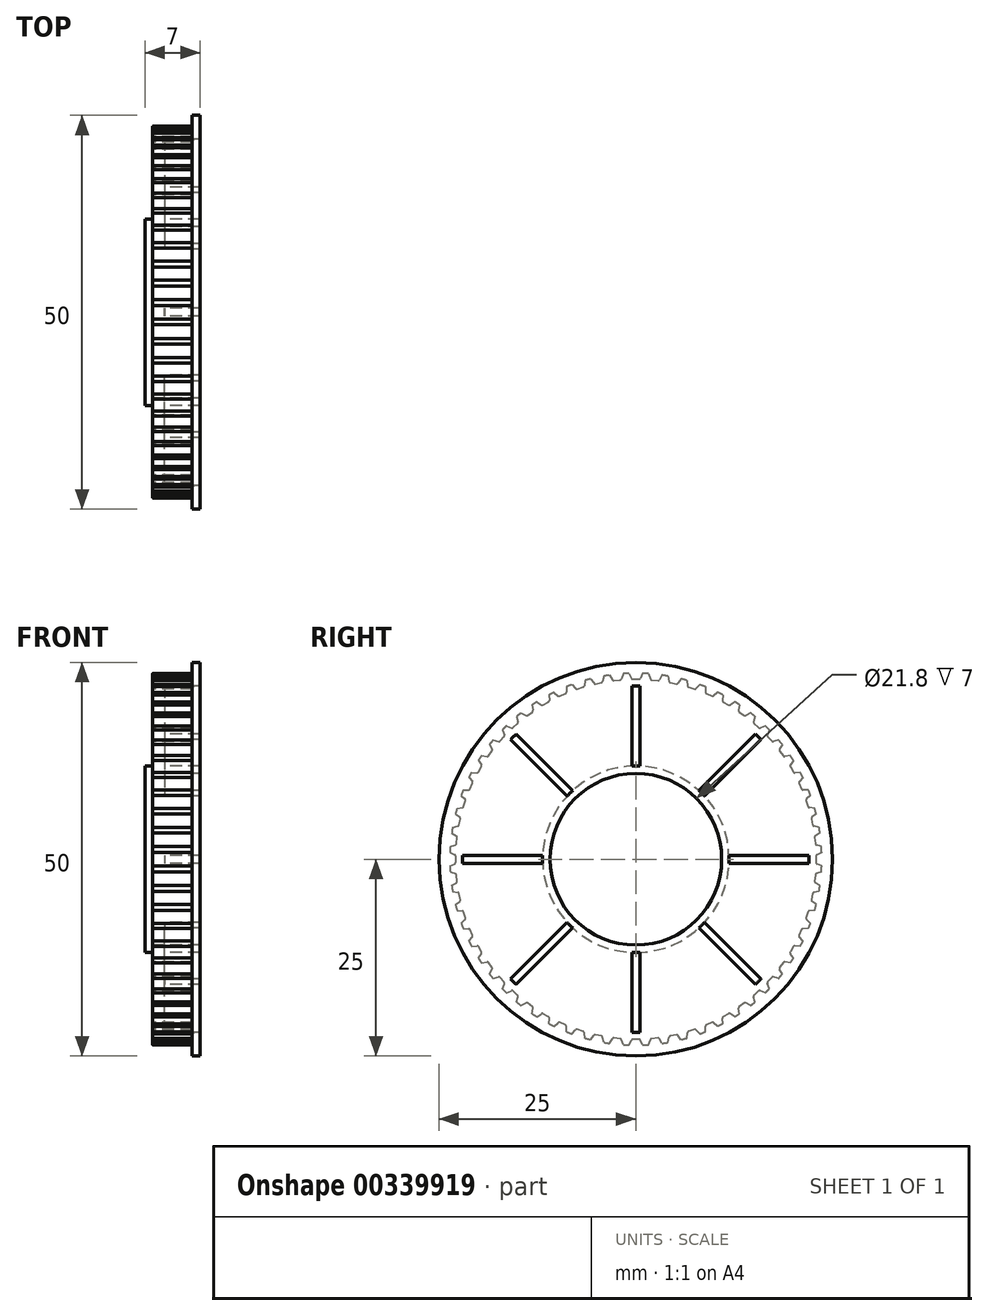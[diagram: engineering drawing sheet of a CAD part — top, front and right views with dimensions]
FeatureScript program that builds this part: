
annotation { "Feature Type Name" : "Feature", "Feature Type Description" : "" }
export const myFeature = defineFeature(function(context is Context, id is Id, definition is map)
    precondition{}
    {
        {
            var Q0;
            Q0=qCreatedBy(makeId("Right.planeOp"),FACE);
            var sketch = newSketch(context, id + "F0", { "sketchPlane" : qUnion([Q0])});
            skCircle(sketch, "E0.0", {"center": v(0, 0) * mm, "radius": 17.8 * mm});
            skCircle(sketch, "E1", {"center": v(0, 0) * mm, "radius": 25 * mm});
            skCircle(sketch, "E2", {"center": v(0, 0) * mm, "radius": 23.86 * mm});
            skCircle(sketch, "E3", {"center": v(0, 0) * mm, "radius": 23.62 * mm});
            skLineSegment(sketch, "E4", {"start": v(-0.88, 23.62) * mm, "end": v(0.87, 23.62) * mm});
            skLineSegment(sketch, "E5", {"start": v(0, 18.78) * mm, "end": v(0, 27.09) * mm, "construction": true});
            skLineSegment(sketch, "E6", {"start": v(-0.4, 22.88) * mm, "end": v(0.4, 22.88) * mm});
            skLineSegment(sketch, "E7", {"start": v(-0.87, 23.62) * mm, "end": v(-0.58, 23) * mm});
            skLineSegment(sketch, "E8", {"start": v(0.87, 23.62) * mm, "end": v(0.58, 23) * mm});
            skArc(sketch, "E9.filletArc", {"start": v(0.4, 22.88) * mm, "mid": v(0.5, 22.9) * mm, "end": v(0.58, 23) * mm});
            skArc(sketch, "E10.filletArc", {"start": v(-0.58, 23) * mm, "mid": v(-0.5, 22.9) * mm, "end": v(-0.4, 22.88) * mm});
            skLineSegment(sketch, "E11.1.0", {"start": v(-1.6, 23.59) * mm, "end": v(-1.83, 22.93) * mm});
            skLineSegment(sketch, "E11.1.1", {"start": v(-3.34, 23.4) * mm, "end": v(-1.6, 23.59) * mm});
            skLineSegment(sketch, "E11.1.2", {"start": v(-2.79, 22.7) * mm, "end": v(-2, 22.8) * mm});
            skLineSegment(sketch, "E11.1.3", {"start": v(-3.34, 23.4) * mm, "end": v(-2.98, 22.8) * mm});
            skArc(sketch, "E11.1.4", {"start": v(-2, 22.8) * mm, "mid": v(-1.9, 22.83) * mm, "end": v(-1.83, 22.93) * mm});
            skArc(sketch, "E11.1.5", {"start": v(-2.98, 22.8) * mm, "mid": v(-2.9, 22.73) * mm, "end": v(-2.79, 22.7) * mm});
            skLineSegment(sketch, "E11.2.0", {"start": v(-4.06, 23.3) * mm, "end": v(-4.21, 22.6) * mm});
            skLineSegment(sketch, "E11.2.1", {"start": v(-5.77, 22.93) * mm, "end": v(-4.06, 23.3) * mm});
            skLineSegment(sketch, "E11.2.2", {"start": v(-5.15, 22.3) * mm, "end": v(-4.37, 22.46) * mm});
            skLineSegment(sketch, "E11.2.3", {"start": v(-5.77, 22.93) * mm, "end": v(-5.35, 22.37) * mm});
            skArc(sketch, "E11.2.4", {"start": v(-4.37, 22.46) * mm, "mid": v(-4.27, 22.51) * mm, "end": v(-4.21, 22.6) * mm});
            skArc(sketch, "E11.2.5", {"start": v(-5.35, 22.37) * mm, "mid": v(-5.26, 22.3) * mm, "end": v(-5.15, 22.3) * mm});
            skLineSegment(sketch, "E11.3.0", {"start": v(-6.47, 22.74) * mm, "end": v(-6.55, 22.04) * mm});
            skLineSegment(sketch, "E11.3.1", {"start": v(-8.13, 22.2) * mm, "end": v(-6.47, 22.74) * mm});
            skLineSegment(sketch, "E11.3.2", {"start": v(-7.45, 21.63) * mm, "end": v(-6.7, 21.88) * mm});
            skLineSegment(sketch, "E11.3.3", {"start": v(-8.13, 22.2) * mm, "end": v(-7.66, 21.69) * mm});
            skArc(sketch, "E11.3.4", {"start": v(-6.7, 21.88) * mm, "mid": v(-6.6, 21.94) * mm, "end": v(-6.55, 22.04) * mm});
            skArc(sketch, "E11.3.5", {"start": v(-7.66, 21.69) * mm, "mid": v(-7.56, 21.63) * mm, "end": v(-7.45, 21.63) * mm});
            skLineSegment(sketch, "E11.4.0", {"start": v(-8.8, 21.94) * mm, "end": v(-8.82, 21.24) * mm});
            skLineSegment(sketch, "E11.4.1", {"start": v(-10.4, 21.23) * mm, "end": v(-8.8, 21.94) * mm});
            skLineSegment(sketch, "E11.4.2", {"start": v(-9.67, 20.74) * mm, "end": v(-8.94, 21.06) * mm});
            skLineSegment(sketch, "E11.4.3", {"start": v(-10.4, 21.23) * mm, "end": v(-9.88, 20.77) * mm});
            skArc(sketch, "E11.4.4", {"start": v(-8.94, 21.06) * mm, "mid": v(-8.86, 21.13) * mm, "end": v(-8.82, 21.24) * mm});
            skArc(sketch, "E11.4.5", {"start": v(-9.88, 20.77) * mm, "mid": v(-9.78, 20.72) * mm, "end": v(-9.67, 20.74) * mm});
            skLineSegment(sketch, "E11.5.0", {"start": v(-11.05, 20.9) * mm, "end": v(-11, 20.2) * mm});
            skLineSegment(sketch, "E11.5.1", {"start": v(-12.57, 20.02) * mm, "end": v(-11.05, 20.9) * mm});
            skLineSegment(sketch, "E11.5.2", {"start": v(-11.78, 19.61) * mm, "end": v(-11.1, 20) * mm});
            skLineSegment(sketch, "E11.5.3", {"start": v(-12.57, 20.02) * mm, "end": v(-12, 19.62) * mm});
            skArc(sketch, "E11.5.4", {"start": v(-11.1, 20) * mm, "mid": v(-11.02, 20.1) * mm, "end": v(-11, 20.2) * mm});
            skArc(sketch, "E11.5.5", {"start": v(-12, 19.62) * mm, "mid": v(-11.9, 19.58) * mm, "end": v(-11.78, 19.61) * mm});
            skLineSegment(sketch, "E11.6.0", {"start": v(-13.18, 19.63) * mm, "end": v(-13.04, 18.94) * mm});
            skLineSegment(sketch, "E11.6.1", {"start": v(-14.6, 18.6) * mm, "end": v(-13.18, 19.63) * mm});
            skLineSegment(sketch, "E11.6.2", {"start": v(-13.77, 18.27) * mm, "end": v(-13.12, 18.74) * mm});
            skLineSegment(sketch, "E11.6.3", {"start": v(-14.6, 18.6) * mm, "end": v(-13.98, 18.26) * mm});
            skArc(sketch, "E11.6.4", {"start": v(-13.12, 18.74) * mm, "mid": v(-13.06, 18.83) * mm, "end": v(-13.04, 18.94) * mm});
            skArc(sketch, "E11.6.5", {"start": v(-13.98, 18.26) * mm, "mid": v(-13.87, 18.23) * mm, "end": v(-13.77, 18.27) * mm});
            skLineSegment(sketch, "E11.7.0", {"start": v(-15.16, 18.14) * mm, "end": v(-14.95, 17.47) * mm});
            skLineSegment(sketch, "E11.7.1", {"start": v(-16.46, 16.97) * mm, "end": v(-15.16, 18.14) * mm});
            skLineSegment(sketch, "E11.7.2", {"start": v(-15.6, 16.73) * mm, "end": v(-15.01, 17.27) * mm});
            skLineSegment(sketch, "E11.7.3", {"start": v(-16.46, 16.97) * mm, "end": v(-15.81, 16.7) * mm});
            skArc(sketch, "E11.7.4", {"start": v(-15.01, 17.27) * mm, "mid": v(-14.95, 17.36) * mm, "end": v(-14.95, 17.47) * mm});
            skArc(sketch, "E11.7.5", {"start": v(-15.81, 16.7) * mm, "mid": v(-15.7, 16.68) * mm, "end": v(-15.6, 16.73) * mm});
            skLineSegment(sketch, "E11.8.0", {"start": v(-16.97, 16.46) * mm, "end": v(-16.7, 15.81) * mm});
            skLineSegment(sketch, "E11.8.1", {"start": v(-18.14, 15.16) * mm, "end": v(-16.97, 16.46) * mm});
            skLineSegment(sketch, "E11.8.2", {"start": v(-17.27, 15.01) * mm, "end": v(-16.73, 15.6) * mm});
            skLineSegment(sketch, "E11.8.3", {"start": v(-18.14, 15.16) * mm, "end": v(-17.47, 14.95) * mm});
            skArc(sketch, "E11.8.4", {"start": v(-16.73, 15.6) * mm, "mid": v(-16.68, 15.7) * mm, "end": v(-16.7, 15.81) * mm});
            skArc(sketch, "E11.8.5", {"start": v(-17.47, 14.95) * mm, "mid": v(-17.36, 14.95) * mm, "end": v(-17.27, 15.01) * mm});
            skLineSegment(sketch, "E11.9.0", {"start": v(-18.6, 14.6) * mm, "end": v(-18.26, 13.98) * mm});
            skLineSegment(sketch, "E11.9.1", {"start": v(-19.63, 13.18) * mm, "end": v(-18.6, 14.6) * mm});
            skLineSegment(sketch, "E11.9.2", {"start": v(-18.74, 13.12) * mm, "end": v(-18.27, 13.77) * mm});
            skLineSegment(sketch, "E11.9.3", {"start": v(-19.63, 13.18) * mm, "end": v(-18.94, 13.04) * mm});
            skArc(sketch, "E11.9.4", {"start": v(-18.27, 13.77) * mm, "mid": v(-18.23, 13.87) * mm, "end": v(-18.26, 13.98) * mm});
            skArc(sketch, "E11.9.5", {"start": v(-18.94, 13.04) * mm, "mid": v(-18.83, 13.06) * mm, "end": v(-18.74, 13.12) * mm});
            skLineSegment(sketch, "E11.10.0", {"start": v(-20.02, 12.57) * mm, "end": v(-19.62, 12) * mm});
            skLineSegment(sketch, "E11.10.1", {"start": v(-20.9, 11.05) * mm, "end": v(-20.02, 12.57) * mm});
            skLineSegment(sketch, "E11.10.2", {"start": v(-20, 11.1) * mm, "end": v(-19.61, 11.78) * mm});
            skLineSegment(sketch, "E11.10.3", {"start": v(-20.9, 11.05) * mm, "end": v(-20.2, 11) * mm});
            skArc(sketch, "E11.10.4", {"start": v(-19.61, 11.78) * mm, "mid": v(-19.58, 11.9) * mm, "end": v(-19.62, 12) * mm});
            skArc(sketch, "E11.10.5", {"start": v(-20.2, 11) * mm, "mid": v(-20.1, 11.02) * mm, "end": v(-20, 11.1) * mm});
            skLineSegment(sketch, "E11.11.0", {"start": v(-21.23, 10.4) * mm, "end": v(-20.77, 9.88) * mm});
            skLineSegment(sketch, "E11.11.1", {"start": v(-21.94, 8.8) * mm, "end": v(-21.23, 10.4) * mm});
            skLineSegment(sketch, "E11.11.2", {"start": v(-21.06, 8.94) * mm, "end": v(-20.74, 9.67) * mm});
            skLineSegment(sketch, "E11.11.3", {"start": v(-21.94, 8.8) * mm, "end": v(-21.24, 8.82) * mm});
            skArc(sketch, "E11.11.4", {"start": v(-20.74, 9.67) * mm, "mid": v(-20.72, 9.78) * mm, "end": v(-20.77, 9.88) * mm});
            skArc(sketch, "E11.11.5", {"start": v(-21.24, 8.82) * mm, "mid": v(-21.13, 8.86) * mm, "end": v(-21.06, 8.94) * mm});
            skLineSegment(sketch, "E11.12.0", {"start": v(-22.2, 8.13) * mm, "end": v(-21.69, 7.66) * mm});
            skLineSegment(sketch, "E11.12.1", {"start": v(-22.74, 6.47) * mm, "end": v(-22.2, 8.13) * mm});
            skLineSegment(sketch, "E11.12.2", {"start": v(-21.88, 6.7) * mm, "end": v(-21.63, 7.45) * mm});
            skLineSegment(sketch, "E11.12.3", {"start": v(-22.74, 6.47) * mm, "end": v(-22.04, 6.55) * mm});
            skArc(sketch, "E11.12.4", {"start": v(-21.63, 7.45) * mm, "mid": v(-21.63, 7.56) * mm, "end": v(-21.69, 7.66) * mm});
            skArc(sketch, "E11.12.5", {"start": v(-22.04, 6.55) * mm, "mid": v(-21.94, 6.6) * mm, "end": v(-21.88, 6.7) * mm});
            skLineSegment(sketch, "E11.13.0", {"start": v(-22.93, 5.77) * mm, "end": v(-22.37, 5.35) * mm});
            skLineSegment(sketch, "E11.13.1", {"start": v(-23.3, 4.06) * mm, "end": v(-22.93, 5.77) * mm});
            skLineSegment(sketch, "E11.13.2", {"start": v(-22.46, 4.37) * mm, "end": v(-22.3, 5.15) * mm});
            skLineSegment(sketch, "E11.13.3", {"start": v(-23.3, 4.06) * mm, "end": v(-22.6, 4.21) * mm});
            skArc(sketch, "E11.13.4", {"start": v(-22.3, 5.15) * mm, "mid": v(-22.3, 5.26) * mm, "end": v(-22.37, 5.35) * mm});
            skArc(sketch, "E11.13.5", {"start": v(-22.6, 4.21) * mm, "mid": v(-22.51, 4.27) * mm, "end": v(-22.46, 4.37) * mm});
            skLineSegment(sketch, "E11.14.0", {"start": v(-23.4, 3.34) * mm, "end": v(-22.8, 2.98) * mm});
            skLineSegment(sketch, "E11.14.1", {"start": v(-23.59, 1.6) * mm, "end": v(-23.4, 3.34) * mm});
            skLineSegment(sketch, "E11.14.2", {"start": v(-22.8, 2) * mm, "end": v(-22.7, 2.79) * mm});
            skLineSegment(sketch, "E11.14.3", {"start": v(-23.59, 1.6) * mm, "end": v(-22.93, 1.83) * mm});
            skArc(sketch, "E11.14.4", {"start": v(-22.7, 2.79) * mm, "mid": v(-22.73, 2.9) * mm, "end": v(-22.8, 2.98) * mm});
            skArc(sketch, "E11.14.5", {"start": v(-22.93, 1.83) * mm, "mid": v(-22.83, 1.9) * mm, "end": v(-22.8, 2) * mm});
            skLineSegment(sketch, "E11.15.0", {"start": v(-23.62, 0.88) * mm, "end": v(-23, 0.58) * mm});
            skLineSegment(sketch, "E11.15.1", {"start": v(-23.62, -0.87) * mm, "end": v(-23.62, 0.88) * mm});
            skLineSegment(sketch, "E11.15.2", {"start": v(-22.88, -0.4) * mm, "end": v(-22.88, 0.4) * mm});
            skLineSegment(sketch, "E11.15.3", {"start": v(-23.62, -0.87) * mm, "end": v(-23, -0.58) * mm});
            skArc(sketch, "E11.15.4", {"start": v(-22.88, 0.4) * mm, "mid": v(-22.9, 0.5) * mm, "end": v(-23, 0.58) * mm});
            skArc(sketch, "E11.15.5", {"start": v(-23, -0.58) * mm, "mid": v(-22.9, -0.5) * mm, "end": v(-22.88, -0.4) * mm});
            skLineSegment(sketch, "E11.16.0", {"start": v(-23.59, -1.6) * mm, "end": v(-22.93, -1.83) * mm});
            skLineSegment(sketch, "E11.16.1", {"start": v(-23.4, -3.34) * mm, "end": v(-23.59, -1.6) * mm});
            skLineSegment(sketch, "E11.16.2", {"start": v(-22.7, -2.79) * mm, "end": v(-22.8, -2) * mm});
            skLineSegment(sketch, "E11.16.3", {"start": v(-23.4, -3.34) * mm, "end": v(-22.8, -2.98) * mm});
            skArc(sketch, "E11.16.4", {"start": v(-22.8, -2) * mm, "mid": v(-22.83, -1.9) * mm, "end": v(-22.93, -1.83) * mm});
            skArc(sketch, "E11.16.5", {"start": v(-22.8, -2.98) * mm, "mid": v(-22.73, -2.9) * mm, "end": v(-22.7, -2.79) * mm});
            skLineSegment(sketch, "E11.17.0", {"start": v(-23.3, -4.06) * mm, "end": v(-22.6, -4.21) * mm});
            skLineSegment(sketch, "E11.17.1", {"start": v(-22.93, -5.77) * mm, "end": v(-23.3, -4.06) * mm});
            skLineSegment(sketch, "E11.17.2", {"start": v(-22.3, -5.15) * mm, "end": v(-22.46, -4.37) * mm});
            skLineSegment(sketch, "E11.17.3", {"start": v(-22.93, -5.77) * mm, "end": v(-22.37, -5.35) * mm});
            skArc(sketch, "E11.17.4", {"start": v(-22.46, -4.37) * mm, "mid": v(-22.51, -4.27) * mm, "end": v(-22.6, -4.21) * mm});
            skArc(sketch, "E11.17.5", {"start": v(-22.37, -5.35) * mm, "mid": v(-22.3, -5.26) * mm, "end": v(-22.3, -5.15) * mm});
            skLineSegment(sketch, "E11.18.0", {"start": v(-22.74, -6.47) * mm, "end": v(-22.04, -6.55) * mm});
            skLineSegment(sketch, "E11.18.1", {"start": v(-22.2, -8.13) * mm, "end": v(-22.74, -6.47) * mm});
            skLineSegment(sketch, "E11.18.2", {"start": v(-21.63, -7.45) * mm, "end": v(-21.88, -6.7) * mm});
            skLineSegment(sketch, "E11.18.3", {"start": v(-22.2, -8.13) * mm, "end": v(-21.69, -7.66) * mm});
            skArc(sketch, "E11.18.4", {"start": v(-21.88, -6.7) * mm, "mid": v(-21.94, -6.6) * mm, "end": v(-22.04, -6.55) * mm});
            skArc(sketch, "E11.18.5", {"start": v(-21.69, -7.66) * mm, "mid": v(-21.63, -7.56) * mm, "end": v(-21.63, -7.45) * mm});
            skLineSegment(sketch, "E11.19.0", {"start": v(-21.94, -8.8) * mm, "end": v(-21.24, -8.82) * mm});
            skLineSegment(sketch, "E11.19.1", {"start": v(-21.23, -10.4) * mm, "end": v(-21.94, -8.8) * mm});
            skLineSegment(sketch, "E11.19.2", {"start": v(-20.74, -9.67) * mm, "end": v(-21.06, -8.94) * mm});
            skLineSegment(sketch, "E11.19.3", {"start": v(-21.23, -10.4) * mm, "end": v(-20.77, -9.88) * mm});
            skArc(sketch, "E11.19.4", {"start": v(-21.06, -8.94) * mm, "mid": v(-21.13, -8.86) * mm, "end": v(-21.24, -8.82) * mm});
            skArc(sketch, "E11.19.5", {"start": v(-20.77, -9.88) * mm, "mid": v(-20.72, -9.78) * mm, "end": v(-20.74, -9.67) * mm});
            skLineSegment(sketch, "E11.20.0", {"start": v(-20.9, -11.05) * mm, "end": v(-20.2, -11) * mm});
            skLineSegment(sketch, "E11.20.1", {"start": v(-20.02, -12.57) * mm, "end": v(-20.9, -11.05) * mm});
            skLineSegment(sketch, "E11.20.2", {"start": v(-19.61, -11.78) * mm, "end": v(-20, -11.1) * mm});
            skLineSegment(sketch, "E11.20.3", {"start": v(-20.02, -12.57) * mm, "end": v(-19.62, -12) * mm});
            skArc(sketch, "E11.20.4", {"start": v(-20, -11.1) * mm, "mid": v(-20.1, -11.02) * mm, "end": v(-20.2, -11) * mm});
            skArc(sketch, "E11.20.5", {"start": v(-19.62, -12) * mm, "mid": v(-19.58, -11.9) * mm, "end": v(-19.61, -11.78) * mm});
            skLineSegment(sketch, "E11.21.0", {"start": v(-19.63, -13.18) * mm, "end": v(-18.94, -13.04) * mm});
            skLineSegment(sketch, "E11.21.1", {"start": v(-18.6, -14.6) * mm, "end": v(-19.63, -13.18) * mm});
            skLineSegment(sketch, "E11.21.2", {"start": v(-18.27, -13.77) * mm, "end": v(-18.74, -13.12) * mm});
            skLineSegment(sketch, "E11.21.3", {"start": v(-18.6, -14.6) * mm, "end": v(-18.26, -13.98) * mm});
            skArc(sketch, "E11.21.4", {"start": v(-18.74, -13.12) * mm, "mid": v(-18.83, -13.06) * mm, "end": v(-18.94, -13.04) * mm});
            skArc(sketch, "E11.21.5", {"start": v(-18.26, -13.98) * mm, "mid": v(-18.23, -13.87) * mm, "end": v(-18.27, -13.77) * mm});
            skLineSegment(sketch, "E11.22.0", {"start": v(-18.14, -15.16) * mm, "end": v(-17.47, -14.95) * mm});
            skLineSegment(sketch, "E11.22.1", {"start": v(-16.97, -16.46) * mm, "end": v(-18.14, -15.16) * mm});
            skLineSegment(sketch, "E11.22.2", {"start": v(-16.73, -15.6) * mm, "end": v(-17.27, -15.01) * mm});
            skLineSegment(sketch, "E11.22.3", {"start": v(-16.97, -16.46) * mm, "end": v(-16.7, -15.81) * mm});
            skArc(sketch, "E11.22.4", {"start": v(-17.27, -15.01) * mm, "mid": v(-17.36, -14.95) * mm, "end": v(-17.47, -14.95) * mm});
            skArc(sketch, "E11.22.5", {"start": v(-16.7, -15.81) * mm, "mid": v(-16.68, -15.7) * mm, "end": v(-16.73, -15.6) * mm});
            skLineSegment(sketch, "E11.23.0", {"start": v(-16.46, -16.97) * mm, "end": v(-15.81, -16.7) * mm});
            skLineSegment(sketch, "E11.23.1", {"start": v(-15.16, -18.14) * mm, "end": v(-16.46, -16.97) * mm});
            skLineSegment(sketch, "E11.23.2", {"start": v(-15.01, -17.27) * mm, "end": v(-15.6, -16.73) * mm});
            skLineSegment(sketch, "E11.23.3", {"start": v(-15.16, -18.14) * mm, "end": v(-14.95, -17.47) * mm});
            skArc(sketch, "E11.23.4", {"start": v(-15.6, -16.73) * mm, "mid": v(-15.7, -16.68) * mm, "end": v(-15.81, -16.7) * mm});
            skArc(sketch, "E11.23.5", {"start": v(-14.95, -17.47) * mm, "mid": v(-14.95, -17.36) * mm, "end": v(-15.01, -17.27) * mm});
            skLineSegment(sketch, "E11.24.0", {"start": v(-14.6, -18.6) * mm, "end": v(-13.98, -18.26) * mm});
            skLineSegment(sketch, "E11.24.1", {"start": v(-13.18, -19.63) * mm, "end": v(-14.6, -18.6) * mm});
            skLineSegment(sketch, "E11.24.2", {"start": v(-13.12, -18.74) * mm, "end": v(-13.77, -18.27) * mm});
            skLineSegment(sketch, "E11.24.3", {"start": v(-13.18, -19.63) * mm, "end": v(-13.04, -18.94) * mm});
            skArc(sketch, "E11.24.4", {"start": v(-13.77, -18.27) * mm, "mid": v(-13.87, -18.23) * mm, "end": v(-13.98, -18.26) * mm});
            skArc(sketch, "E11.24.5", {"start": v(-13.04, -18.94) * mm, "mid": v(-13.06, -18.83) * mm, "end": v(-13.12, -18.74) * mm});
            skLineSegment(sketch, "E11.25.0", {"start": v(-12.57, -20.02) * mm, "end": v(-12, -19.62) * mm});
            skLineSegment(sketch, "E11.25.1", {"start": v(-11.05, -20.9) * mm, "end": v(-12.57, -20.02) * mm});
            skLineSegment(sketch, "E11.25.2", {"start": v(-11.1, -20) * mm, "end": v(-11.78, -19.61) * mm});
            skLineSegment(sketch, "E11.25.3", {"start": v(-11.05, -20.9) * mm, "end": v(-11, -20.2) * mm});
            skArc(sketch, "E11.25.4", {"start": v(-11.78, -19.61) * mm, "mid": v(-11.9, -19.58) * mm, "end": v(-12, -19.62) * mm});
            skArc(sketch, "E11.25.5", {"start": v(-11, -20.2) * mm, "mid": v(-11.02, -20.1) * mm, "end": v(-11.1, -20) * mm});
            skLineSegment(sketch, "E11.26.0", {"start": v(-10.4, -21.23) * mm, "end": v(-9.88, -20.77) * mm});
            skLineSegment(sketch, "E11.26.1", {"start": v(-8.8, -21.94) * mm, "end": v(-10.4, -21.23) * mm});
            skLineSegment(sketch, "E11.26.2", {"start": v(-8.94, -21.06) * mm, "end": v(-9.67, -20.74) * mm});
            skLineSegment(sketch, "E11.26.3", {"start": v(-8.8, -21.94) * mm, "end": v(-8.82, -21.24) * mm});
            skArc(sketch, "E11.26.4", {"start": v(-9.67, -20.74) * mm, "mid": v(-9.78, -20.72) * mm, "end": v(-9.88, -20.77) * mm});
            skArc(sketch, "E11.26.5", {"start": v(-8.82, -21.24) * mm, "mid": v(-8.86, -21.13) * mm, "end": v(-8.94, -21.06) * mm});
            skLineSegment(sketch, "E11.27.0", {"start": v(-8.13, -22.2) * mm, "end": v(-7.66, -21.69) * mm});
            skLineSegment(sketch, "E11.27.1", {"start": v(-6.47, -22.74) * mm, "end": v(-8.13, -22.2) * mm});
            skLineSegment(sketch, "E11.27.2", {"start": v(-6.7, -21.88) * mm, "end": v(-7.45, -21.63) * mm});
            skLineSegment(sketch, "E11.27.3", {"start": v(-6.47, -22.74) * mm, "end": v(-6.55, -22.04) * mm});
            skArc(sketch, "E11.27.4", {"start": v(-7.45, -21.63) * mm, "mid": v(-7.56, -21.63) * mm, "end": v(-7.66, -21.69) * mm});
            skArc(sketch, "E11.27.5", {"start": v(-6.55, -22.04) * mm, "mid": v(-6.6, -21.94) * mm, "end": v(-6.7, -21.88) * mm});
            skLineSegment(sketch, "E11.28.0", {"start": v(-5.77, -22.93) * mm, "end": v(-5.35, -22.37) * mm});
            skLineSegment(sketch, "E11.28.1", {"start": v(-4.06, -23.3) * mm, "end": v(-5.77, -22.93) * mm});
            skLineSegment(sketch, "E11.28.2", {"start": v(-4.37, -22.46) * mm, "end": v(-5.15, -22.3) * mm});
            skLineSegment(sketch, "E11.28.3", {"start": v(-4.06, -23.3) * mm, "end": v(-4.21, -22.6) * mm});
            skArc(sketch, "E11.28.4", {"start": v(-5.15, -22.3) * mm, "mid": v(-5.26, -22.3) * mm, "end": v(-5.35, -22.37) * mm});
            skArc(sketch, "E11.28.5", {"start": v(-4.21, -22.6) * mm, "mid": v(-4.27, -22.51) * mm, "end": v(-4.37, -22.46) * mm});
            skLineSegment(sketch, "E11.29.0", {"start": v(-3.34, -23.4) * mm, "end": v(-2.98, -22.8) * mm});
            skLineSegment(sketch, "E11.29.1", {"start": v(-1.6, -23.59) * mm, "end": v(-3.34, -23.4) * mm});
            skLineSegment(sketch, "E11.29.2", {"start": v(-2, -22.8) * mm, "end": v(-2.79, -22.7) * mm});
            skLineSegment(sketch, "E11.29.3", {"start": v(-1.6, -23.59) * mm, "end": v(-1.83, -22.93) * mm});
            skArc(sketch, "E11.29.4", {"start": v(-2.79, -22.7) * mm, "mid": v(-2.9, -22.73) * mm, "end": v(-2.98, -22.8) * mm});
            skArc(sketch, "E11.29.5", {"start": v(-1.83, -22.93) * mm, "mid": v(-1.9, -22.83) * mm, "end": v(-2, -22.8) * mm});
            skLineSegment(sketch, "E11.30.0", {"start": v(-0.88, -23.62) * mm, "end": v(-0.58, -23) * mm});
            skLineSegment(sketch, "E11.30.1", {"start": v(0.87, -23.62) * mm, "end": v(-0.88, -23.62) * mm});
            skLineSegment(sketch, "E11.30.2", {"start": v(0.4, -22.88) * mm, "end": v(-0.4, -22.88) * mm});
            skLineSegment(sketch, "E11.30.3", {"start": v(0.87, -23.62) * mm, "end": v(0.58, -23) * mm});
            skArc(sketch, "E11.30.4", {"start": v(-0.4, -22.88) * mm, "mid": v(-0.5, -22.9) * mm, "end": v(-0.58, -23) * mm});
            skArc(sketch, "E11.30.5", {"start": v(0.58, -23) * mm, "mid": v(0.5, -22.9) * mm, "end": v(0.4, -22.88) * mm});
            skLineSegment(sketch, "E11.31.0", {"start": v(1.6, -23.59) * mm, "end": v(1.83, -22.93) * mm});
            skLineSegment(sketch, "E11.31.1", {"start": v(3.34, -23.4) * mm, "end": v(1.6, -23.59) * mm});
            skLineSegment(sketch, "E11.31.2", {"start": v(2.79, -22.7) * mm, "end": v(2, -22.8) * mm});
            skLineSegment(sketch, "E11.31.3", {"start": v(3.34, -23.4) * mm, "end": v(2.98, -22.8) * mm});
            skArc(sketch, "E11.31.4", {"start": v(2, -22.8) * mm, "mid": v(1.9, -22.83) * mm, "end": v(1.83, -22.93) * mm});
            skArc(sketch, "E11.31.5", {"start": v(2.98, -22.8) * mm, "mid": v(2.9, -22.73) * mm, "end": v(2.79, -22.7) * mm});
            skLineSegment(sketch, "E11.32.0", {"start": v(4.06, -23.3) * mm, "end": v(4.21, -22.6) * mm});
            skLineSegment(sketch, "E11.32.1", {"start": v(5.77, -22.93) * mm, "end": v(4.06, -23.3) * mm});
            skLineSegment(sketch, "E11.32.2", {"start": v(5.15, -22.3) * mm, "end": v(4.37, -22.46) * mm});
            skLineSegment(sketch, "E11.32.3", {"start": v(5.77, -22.93) * mm, "end": v(5.35, -22.37) * mm});
            skArc(sketch, "E11.32.4", {"start": v(4.37, -22.46) * mm, "mid": v(4.27, -22.51) * mm, "end": v(4.21, -22.6) * mm});
            skArc(sketch, "E11.32.5", {"start": v(5.35, -22.37) * mm, "mid": v(5.26, -22.3) * mm, "end": v(5.15, -22.3) * mm});
            skLineSegment(sketch, "E11.33.0", {"start": v(6.47, -22.74) * mm, "end": v(6.55, -22.04) * mm});
            skLineSegment(sketch, "E11.33.1", {"start": v(8.13, -22.2) * mm, "end": v(6.47, -22.74) * mm});
            skLineSegment(sketch, "E11.33.2", {"start": v(7.45, -21.63) * mm, "end": v(6.7, -21.88) * mm});
            skLineSegment(sketch, "E11.33.3", {"start": v(8.13, -22.2) * mm, "end": v(7.66, -21.69) * mm});
            skArc(sketch, "E11.33.4", {"start": v(6.7, -21.88) * mm, "mid": v(6.6, -21.94) * mm, "end": v(6.55, -22.04) * mm});
            skArc(sketch, "E11.33.5", {"start": v(7.66, -21.69) * mm, "mid": v(7.56, -21.63) * mm, "end": v(7.45, -21.63) * mm});
            skLineSegment(sketch, "E11.34.0", {"start": v(8.8, -21.94) * mm, "end": v(8.82, -21.24) * mm});
            skLineSegment(sketch, "E11.34.1", {"start": v(10.4, -21.23) * mm, "end": v(8.8, -21.94) * mm});
            skLineSegment(sketch, "E11.34.2", {"start": v(9.67, -20.74) * mm, "end": v(8.94, -21.06) * mm});
            skLineSegment(sketch, "E11.34.3", {"start": v(10.4, -21.23) * mm, "end": v(9.88, -20.77) * mm});
            skArc(sketch, "E11.34.4", {"start": v(8.94, -21.06) * mm, "mid": v(8.86, -21.13) * mm, "end": v(8.82, -21.24) * mm});
            skArc(sketch, "E11.34.5", {"start": v(9.88, -20.77) * mm, "mid": v(9.78, -20.72) * mm, "end": v(9.67, -20.74) * mm});
            skLineSegment(sketch, "E11.35.0", {"start": v(11.05, -20.9) * mm, "end": v(11, -20.2) * mm});
            skLineSegment(sketch, "E11.35.1", {"start": v(12.57, -20.02) * mm, "end": v(11.05, -20.9) * mm});
            skLineSegment(sketch, "E11.35.2", {"start": v(11.78, -19.61) * mm, "end": v(11.1, -20) * mm});
            skLineSegment(sketch, "E11.35.3", {"start": v(12.57, -20.02) * mm, "end": v(12, -19.62) * mm});
            skArc(sketch, "E11.35.4", {"start": v(11.1, -20) * mm, "mid": v(11.02, -20.1) * mm, "end": v(11, -20.2) * mm});
            skArc(sketch, "E11.35.5", {"start": v(12, -19.62) * mm, "mid": v(11.9, -19.58) * mm, "end": v(11.78, -19.61) * mm});
            skLineSegment(sketch, "E11.36.0", {"start": v(13.18, -19.63) * mm, "end": v(13.04, -18.94) * mm});
            skLineSegment(sketch, "E11.36.1", {"start": v(14.6, -18.6) * mm, "end": v(13.18, -19.63) * mm});
            skLineSegment(sketch, "E11.36.2", {"start": v(13.77, -18.27) * mm, "end": v(13.12, -18.74) * mm});
            skLineSegment(sketch, "E11.36.3", {"start": v(14.6, -18.6) * mm, "end": v(13.98, -18.26) * mm});
            skArc(sketch, "E11.36.4", {"start": v(13.12, -18.74) * mm, "mid": v(13.06, -18.83) * mm, "end": v(13.04, -18.94) * mm});
            skArc(sketch, "E11.36.5", {"start": v(13.98, -18.26) * mm, "mid": v(13.87, -18.23) * mm, "end": v(13.77, -18.27) * mm});
            skLineSegment(sketch, "E11.37.0", {"start": v(15.16, -18.14) * mm, "end": v(14.95, -17.47) * mm});
            skLineSegment(sketch, "E11.37.1", {"start": v(16.46, -16.97) * mm, "end": v(15.16, -18.14) * mm});
            skLineSegment(sketch, "E11.37.2", {"start": v(15.6, -16.73) * mm, "end": v(15.01, -17.27) * mm});
            skLineSegment(sketch, "E11.37.3", {"start": v(16.46, -16.97) * mm, "end": v(15.81, -16.7) * mm});
            skArc(sketch, "E11.37.4", {"start": v(15.01, -17.27) * mm, "mid": v(14.95, -17.36) * mm, "end": v(14.95, -17.47) * mm});
            skArc(sketch, "E11.37.5", {"start": v(15.81, -16.7) * mm, "mid": v(15.7, -16.68) * mm, "end": v(15.6, -16.73) * mm});
            skLineSegment(sketch, "E11.38.0", {"start": v(16.97, -16.46) * mm, "end": v(16.7, -15.81) * mm});
            skLineSegment(sketch, "E11.38.1", {"start": v(18.14, -15.16) * mm, "end": v(16.97, -16.46) * mm});
            skLineSegment(sketch, "E11.38.2", {"start": v(17.27, -15.01) * mm, "end": v(16.73, -15.6) * mm});
            skLineSegment(sketch, "E11.38.3", {"start": v(18.14, -15.16) * mm, "end": v(17.47, -14.95) * mm});
            skArc(sketch, "E11.38.4", {"start": v(16.73, -15.6) * mm, "mid": v(16.68, -15.7) * mm, "end": v(16.7, -15.81) * mm});
            skArc(sketch, "E11.38.5", {"start": v(17.47, -14.95) * mm, "mid": v(17.36, -14.95) * mm, "end": v(17.27, -15.01) * mm});
            skLineSegment(sketch, "E11.39.0", {"start": v(18.6, -14.6) * mm, "end": v(18.26, -13.98) * mm});
            skLineSegment(sketch, "E11.39.1", {"start": v(19.63, -13.18) * mm, "end": v(18.6, -14.6) * mm});
            skLineSegment(sketch, "E11.39.2", {"start": v(18.74, -13.12) * mm, "end": v(18.27, -13.77) * mm});
            skLineSegment(sketch, "E11.39.3", {"start": v(19.63, -13.18) * mm, "end": v(18.94, -13.04) * mm});
            skArc(sketch, "E11.39.4", {"start": v(18.27, -13.77) * mm, "mid": v(18.23, -13.87) * mm, "end": v(18.26, -13.98) * mm});
            skArc(sketch, "E11.39.5", {"start": v(18.94, -13.04) * mm, "mid": v(18.83, -13.06) * mm, "end": v(18.74, -13.12) * mm});
            skLineSegment(sketch, "E11.40.0", {"start": v(20.02, -12.57) * mm, "end": v(19.62, -12) * mm});
            skLineSegment(sketch, "E11.40.1", {"start": v(20.9, -11.05) * mm, "end": v(20.02, -12.57) * mm});
            skLineSegment(sketch, "E11.40.2", {"start": v(20, -11.1) * mm, "end": v(19.61, -11.78) * mm});
            skLineSegment(sketch, "E11.40.3", {"start": v(20.9, -11.05) * mm, "end": v(20.2, -11) * mm});
            skArc(sketch, "E11.40.4", {"start": v(19.61, -11.78) * mm, "mid": v(19.58, -11.9) * mm, "end": v(19.62, -12) * mm});
            skArc(sketch, "E11.40.5", {"start": v(20.2, -11) * mm, "mid": v(20.1, -11.02) * mm, "end": v(20, -11.1) * mm});
            skLineSegment(sketch, "E11.41.0", {"start": v(21.23, -10.4) * mm, "end": v(20.77, -9.88) * mm});
            skLineSegment(sketch, "E11.41.1", {"start": v(21.94, -8.8) * mm, "end": v(21.23, -10.4) * mm});
            skLineSegment(sketch, "E11.41.2", {"start": v(21.06, -8.94) * mm, "end": v(20.74, -9.67) * mm});
            skLineSegment(sketch, "E11.41.3", {"start": v(21.94, -8.8) * mm, "end": v(21.24, -8.82) * mm});
            skArc(sketch, "E11.41.4", {"start": v(20.74, -9.67) * mm, "mid": v(20.72, -9.78) * mm, "end": v(20.77, -9.88) * mm});
            skArc(sketch, "E11.41.5", {"start": v(21.24, -8.82) * mm, "mid": v(21.13, -8.86) * mm, "end": v(21.06, -8.94) * mm});
            skLineSegment(sketch, "E11.42.0", {"start": v(22.2, -8.13) * mm, "end": v(21.69, -7.66) * mm});
            skLineSegment(sketch, "E11.42.1", {"start": v(22.74, -6.47) * mm, "end": v(22.2, -8.13) * mm});
            skLineSegment(sketch, "E11.42.2", {"start": v(21.88, -6.7) * mm, "end": v(21.63, -7.45) * mm});
            skLineSegment(sketch, "E11.42.3", {"start": v(22.74, -6.47) * mm, "end": v(22.04, -6.55) * mm});
            skArc(sketch, "E11.42.4", {"start": v(21.63, -7.45) * mm, "mid": v(21.63, -7.56) * mm, "end": v(21.69, -7.66) * mm});
            skArc(sketch, "E11.42.5", {"start": v(22.04, -6.55) * mm, "mid": v(21.94, -6.6) * mm, "end": v(21.88, -6.7) * mm});
            skLineSegment(sketch, "E11.43.0", {"start": v(22.93, -5.77) * mm, "end": v(22.37, -5.35) * mm});
            skLineSegment(sketch, "E11.43.1", {"start": v(23.3, -4.06) * mm, "end": v(22.93, -5.77) * mm});
            skLineSegment(sketch, "E11.43.2", {"start": v(22.46, -4.37) * mm, "end": v(22.3, -5.15) * mm});
            skLineSegment(sketch, "E11.43.3", {"start": v(23.3, -4.06) * mm, "end": v(22.6, -4.21) * mm});
            skArc(sketch, "E11.43.4", {"start": v(22.3, -5.15) * mm, "mid": v(22.3, -5.26) * mm, "end": v(22.37, -5.35) * mm});
            skArc(sketch, "E11.43.5", {"start": v(22.6, -4.21) * mm, "mid": v(22.51, -4.27) * mm, "end": v(22.46, -4.37) * mm});
            skLineSegment(sketch, "E11.44.0", {"start": v(23.4, -3.34) * mm, "end": v(22.8, -2.98) * mm});
            skLineSegment(sketch, "E11.44.1", {"start": v(23.59, -1.6) * mm, "end": v(23.4, -3.34) * mm});
            skLineSegment(sketch, "E11.44.2", {"start": v(22.8, -2) * mm, "end": v(22.7, -2.79) * mm});
            skLineSegment(sketch, "E11.44.3", {"start": v(23.59, -1.6) * mm, "end": v(22.93, -1.83) * mm});
            skArc(sketch, "E11.44.4", {"start": v(22.7, -2.79) * mm, "mid": v(22.73, -2.9) * mm, "end": v(22.8, -2.98) * mm});
            skArc(sketch, "E11.44.5", {"start": v(22.93, -1.83) * mm, "mid": v(22.83, -1.9) * mm, "end": v(22.8, -2) * mm});
            skLineSegment(sketch, "E11.45.0", {"start": v(23.62, -0.88) * mm, "end": v(23, -0.58) * mm});
            skLineSegment(sketch, "E11.45.1", {"start": v(23.62, 0.87) * mm, "end": v(23.62, -0.88) * mm});
            skLineSegment(sketch, "E11.45.2", {"start": v(22.88, 0.4) * mm, "end": v(22.88, -0.4) * mm});
            skLineSegment(sketch, "E11.45.3", {"start": v(23.62, 0.87) * mm, "end": v(23, 0.58) * mm});
            skArc(sketch, "E11.45.4", {"start": v(22.88, -0.4) * mm, "mid": v(22.9, -0.5) * mm, "end": v(23, -0.58) * mm});
            skArc(sketch, "E11.45.5", {"start": v(23, 0.58) * mm, "mid": v(22.9, 0.5) * mm, "end": v(22.88, 0.4) * mm});
            skLineSegment(sketch, "E11.46.0", {"start": v(23.59, 1.6) * mm, "end": v(22.93, 1.83) * mm});
            skLineSegment(sketch, "E11.46.1", {"start": v(23.4, 3.34) * mm, "end": v(23.59, 1.6) * mm});
            skLineSegment(sketch, "E11.46.2", {"start": v(22.7, 2.79) * mm, "end": v(22.8, 2) * mm});
            skLineSegment(sketch, "E11.46.3", {"start": v(23.4, 3.34) * mm, "end": v(22.8, 2.98) * mm});
            skArc(sketch, "E11.46.4", {"start": v(22.8, 2) * mm, "mid": v(22.83, 1.9) * mm, "end": v(22.93, 1.83) * mm});
            skArc(sketch, "E11.46.5", {"start": v(22.8, 2.98) * mm, "mid": v(22.73, 2.9) * mm, "end": v(22.7, 2.79) * mm});
            skLineSegment(sketch, "E11.47.0", {"start": v(23.3, 4.06) * mm, "end": v(22.6, 4.21) * mm});
            skLineSegment(sketch, "E11.47.1", {"start": v(22.93, 5.77) * mm, "end": v(23.3, 4.06) * mm});
            skLineSegment(sketch, "E11.47.2", {"start": v(22.3, 5.15) * mm, "end": v(22.46, 4.37) * mm});
            skLineSegment(sketch, "E11.47.3", {"start": v(22.93, 5.77) * mm, "end": v(22.37, 5.35) * mm});
            skArc(sketch, "E11.47.4", {"start": v(22.46, 4.37) * mm, "mid": v(22.51, 4.27) * mm, "end": v(22.6, 4.21) * mm});
            skArc(sketch, "E11.47.5", {"start": v(22.37, 5.35) * mm, "mid": v(22.3, 5.26) * mm, "end": v(22.3, 5.15) * mm});
            skLineSegment(sketch, "E11.48.0", {"start": v(22.74, 6.47) * mm, "end": v(22.04, 6.55) * mm});
            skLineSegment(sketch, "E11.48.1", {"start": v(22.2, 8.13) * mm, "end": v(22.74, 6.47) * mm});
            skLineSegment(sketch, "E11.48.2", {"start": v(21.63, 7.45) * mm, "end": v(21.88, 6.7) * mm});
            skLineSegment(sketch, "E11.48.3", {"start": v(22.2, 8.13) * mm, "end": v(21.69, 7.66) * mm});
            skArc(sketch, "E11.48.4", {"start": v(21.88, 6.7) * mm, "mid": v(21.94, 6.6) * mm, "end": v(22.04, 6.55) * mm});
            skArc(sketch, "E11.48.5", {"start": v(21.69, 7.66) * mm, "mid": v(21.63, 7.56) * mm, "end": v(21.63, 7.45) * mm});
            skLineSegment(sketch, "E11.49.0", {"start": v(21.94, 8.8) * mm, "end": v(21.24, 8.82) * mm});
            skLineSegment(sketch, "E11.49.1", {"start": v(21.23, 10.4) * mm, "end": v(21.94, 8.8) * mm});
            skLineSegment(sketch, "E11.49.2", {"start": v(20.74, 9.67) * mm, "end": v(21.06, 8.94) * mm});
            skLineSegment(sketch, "E11.49.3", {"start": v(21.23, 10.4) * mm, "end": v(20.77, 9.88) * mm});
            skArc(sketch, "E11.49.4", {"start": v(21.06, 8.94) * mm, "mid": v(21.13, 8.86) * mm, "end": v(21.24, 8.82) * mm});
            skArc(sketch, "E11.49.5", {"start": v(20.77, 9.88) * mm, "mid": v(20.72, 9.78) * mm, "end": v(20.74, 9.67) * mm});
            skLineSegment(sketch, "E11.50.0", {"start": v(20.9, 11.05) * mm, "end": v(20.2, 11) * mm});
            skLineSegment(sketch, "E11.50.1", {"start": v(20.02, 12.57) * mm, "end": v(20.9, 11.05) * mm});
            skLineSegment(sketch, "E11.50.2", {"start": v(19.61, 11.78) * mm, "end": v(20, 11.1) * mm});
            skLineSegment(sketch, "E11.50.3", {"start": v(20.02, 12.57) * mm, "end": v(19.62, 12) * mm});
            skArc(sketch, "E11.50.4", {"start": v(20, 11.1) * mm, "mid": v(20.1, 11.02) * mm, "end": v(20.2, 11) * mm});
            skArc(sketch, "E11.50.5", {"start": v(19.62, 12) * mm, "mid": v(19.58, 11.9) * mm, "end": v(19.61, 11.78) * mm});
            skLineSegment(sketch, "E11.51.0", {"start": v(19.63, 13.18) * mm, "end": v(18.94, 13.04) * mm});
            skLineSegment(sketch, "E11.51.1", {"start": v(18.6, 14.6) * mm, "end": v(19.63, 13.18) * mm});
            skLineSegment(sketch, "E11.51.2", {"start": v(18.27, 13.77) * mm, "end": v(18.74, 13.12) * mm});
            skLineSegment(sketch, "E11.51.3", {"start": v(18.6, 14.6) * mm, "end": v(18.26, 13.98) * mm});
            skArc(sketch, "E11.51.4", {"start": v(18.74, 13.12) * mm, "mid": v(18.83, 13.06) * mm, "end": v(18.94, 13.04) * mm});
            skArc(sketch, "E11.51.5", {"start": v(18.26, 13.98) * mm, "mid": v(18.23, 13.87) * mm, "end": v(18.27, 13.77) * mm});
            skLineSegment(sketch, "E11.52.0", {"start": v(18.14, 15.16) * mm, "end": v(17.47, 14.95) * mm});
            skLineSegment(sketch, "E11.52.1", {"start": v(16.97, 16.46) * mm, "end": v(18.14, 15.16) * mm});
            skLineSegment(sketch, "E11.52.2", {"start": v(16.73, 15.6) * mm, "end": v(17.27, 15.01) * mm});
            skLineSegment(sketch, "E11.52.3", {"start": v(16.97, 16.46) * mm, "end": v(16.7, 15.81) * mm});
            skArc(sketch, "E11.52.4", {"start": v(17.27, 15.01) * mm, "mid": v(17.36, 14.95) * mm, "end": v(17.47, 14.95) * mm});
            skArc(sketch, "E11.52.5", {"start": v(16.7, 15.81) * mm, "mid": v(16.68, 15.7) * mm, "end": v(16.73, 15.6) * mm});
            skLineSegment(sketch, "E11.53.0", {"start": v(16.46, 16.97) * mm, "end": v(15.81, 16.7) * mm});
            skLineSegment(sketch, "E11.53.1", {"start": v(15.16, 18.14) * mm, "end": v(16.46, 16.97) * mm});
            skLineSegment(sketch, "E11.53.2", {"start": v(15.01, 17.27) * mm, "end": v(15.6, 16.73) * mm});
            skLineSegment(sketch, "E11.53.3", {"start": v(15.16, 18.14) * mm, "end": v(14.95, 17.47) * mm});
            skArc(sketch, "E11.53.4", {"start": v(15.6, 16.73) * mm, "mid": v(15.7, 16.68) * mm, "end": v(15.81, 16.7) * mm});
            skArc(sketch, "E11.53.5", {"start": v(14.95, 17.47) * mm, "mid": v(14.95, 17.36) * mm, "end": v(15.01, 17.27) * mm});
            skLineSegment(sketch, "E11.54.0", {"start": v(14.6, 18.6) * mm, "end": v(13.98, 18.26) * mm});
            skLineSegment(sketch, "E11.54.1", {"start": v(13.18, 19.63) * mm, "end": v(14.6, 18.6) * mm});
            skLineSegment(sketch, "E11.54.2", {"start": v(13.12, 18.74) * mm, "end": v(13.77, 18.27) * mm});
            skLineSegment(sketch, "E11.54.3", {"start": v(13.18, 19.63) * mm, "end": v(13.04, 18.94) * mm});
            skArc(sketch, "E11.54.4", {"start": v(13.77, 18.27) * mm, "mid": v(13.87, 18.23) * mm, "end": v(13.98, 18.26) * mm});
            skArc(sketch, "E11.54.5", {"start": v(13.04, 18.94) * mm, "mid": v(13.06, 18.83) * mm, "end": v(13.12, 18.74) * mm});
            skLineSegment(sketch, "E11.55.0", {"start": v(12.57, 20.02) * mm, "end": v(12, 19.62) * mm});
            skLineSegment(sketch, "E11.55.1", {"start": v(11.05, 20.9) * mm, "end": v(12.57, 20.02) * mm});
            skLineSegment(sketch, "E11.55.2", {"start": v(11.1, 20) * mm, "end": v(11.78, 19.61) * mm});
            skLineSegment(sketch, "E11.55.3", {"start": v(11.05, 20.9) * mm, "end": v(11, 20.2) * mm});
            skArc(sketch, "E11.55.4", {"start": v(11.78, 19.61) * mm, "mid": v(11.9, 19.58) * mm, "end": v(12, 19.62) * mm});
            skArc(sketch, "E11.55.5", {"start": v(11, 20.2) * mm, "mid": v(11.02, 20.1) * mm, "end": v(11.1, 20) * mm});
            skLineSegment(sketch, "E11.56.0", {"start": v(10.4, 21.23) * mm, "end": v(9.88, 20.77) * mm});
            skLineSegment(sketch, "E11.56.1", {"start": v(8.8, 21.94) * mm, "end": v(10.4, 21.23) * mm});
            skLineSegment(sketch, "E11.56.2", {"start": v(8.94, 21.06) * mm, "end": v(9.67, 20.74) * mm});
            skLineSegment(sketch, "E11.56.3", {"start": v(8.8, 21.94) * mm, "end": v(8.82, 21.24) * mm});
            skArc(sketch, "E11.56.4", {"start": v(9.67, 20.74) * mm, "mid": v(9.78, 20.72) * mm, "end": v(9.88, 20.77) * mm});
            skArc(sketch, "E11.56.5", {"start": v(8.82, 21.24) * mm, "mid": v(8.86, 21.13) * mm, "end": v(8.94, 21.06) * mm});
            skLineSegment(sketch, "E11.57.0", {"start": v(8.13, 22.2) * mm, "end": v(7.66, 21.69) * mm});
            skLineSegment(sketch, "E11.57.1", {"start": v(6.47, 22.74) * mm, "end": v(8.13, 22.2) * mm});
            skLineSegment(sketch, "E11.57.2", {"start": v(6.7, 21.88) * mm, "end": v(7.45, 21.63) * mm});
            skLineSegment(sketch, "E11.57.3", {"start": v(6.47, 22.74) * mm, "end": v(6.55, 22.04) * mm});
            skArc(sketch, "E11.57.4", {"start": v(7.45, 21.63) * mm, "mid": v(7.56, 21.63) * mm, "end": v(7.66, 21.69) * mm});
            skArc(sketch, "E11.57.5", {"start": v(6.55, 22.04) * mm, "mid": v(6.6, 21.94) * mm, "end": v(6.7, 21.88) * mm});
            skLineSegment(sketch, "E11.58.0", {"start": v(5.77, 22.93) * mm, "end": v(5.35, 22.37) * mm});
            skLineSegment(sketch, "E11.58.1", {"start": v(4.06, 23.3) * mm, "end": v(5.77, 22.93) * mm});
            skLineSegment(sketch, "E11.58.2", {"start": v(4.37, 22.46) * mm, "end": v(5.15, 22.3) * mm});
            skLineSegment(sketch, "E11.58.3", {"start": v(4.06, 23.3) * mm, "end": v(4.21, 22.6) * mm});
            skArc(sketch, "E11.58.4", {"start": v(5.15, 22.3) * mm, "mid": v(5.26, 22.3) * mm, "end": v(5.35, 22.37) * mm});
            skArc(sketch, "E11.58.5", {"start": v(4.21, 22.6) * mm, "mid": v(4.27, 22.51) * mm, "end": v(4.37, 22.46) * mm});
            skLineSegment(sketch, "E11.59.0", {"start": v(3.34, 23.4) * mm, "end": v(2.98, 22.8) * mm});
            skLineSegment(sketch, "E11.59.1", {"start": v(1.6, 23.59) * mm, "end": v(3.34, 23.4) * mm});
            skLineSegment(sketch, "E11.59.2", {"start": v(2, 22.8) * mm, "end": v(2.79, 22.7) * mm});
            skLineSegment(sketch, "E11.59.3", {"start": v(1.6, 23.59) * mm, "end": v(1.83, 22.93) * mm});
            skArc(sketch, "E11.59.4", {"start": v(2.79, 22.7) * mm, "mid": v(2.9, 22.73) * mm, "end": v(2.98, 22.8) * mm});
            skArc(sketch, "E11.59.5", {"start": v(1.83, 22.93) * mm, "mid": v(1.9, 22.83) * mm, "end": v(2, 22.8) * mm});
            skCircle(sketch, "E12.0", {"center": v(0, 0) * mm, "radius": 12 * mm});
            skCircle(sketch, "E13", {"center": v(0, 0) * mm, "radius": 10.9 * mm});
            skCircle(sketch, "E14", {"center": v(0, 0) * mm, "radius": 9.7 * mm});
            skSolve(sketch);
        }
        {
            var Q0;
            Q0=makeQuery(id+"F0.imprint","IMPRINT",FACE,{"disambiguationData":[TD([[makeQuery(id+"F0.imprint","IMPRINT",EDGE,{"derivedFrom":sQuery(id+"F0.wireOp",EDGE,"E0.0")}),1.0]])]});
            var Q1;
            Q1=makeQuery(id+"F0.imprint","IMPRINT",FACE,{"disambiguationData":[TD([[makeQuery(id+"F0.imprint","IMPRINT",EDGE,{"derivedFrom":sQuery(id+"F0.wireOp",EDGE,"E0.0")}),-1.0]])]});
            var Q2;
            Q2=makeQuery(id+"F0.imprint","IMPRINT",FACE,{"disambiguationData":[TD([[makeQuery(id+"F0.imprint","IMPRINT",EDGE,{"derivedFrom":sQuery(id+"F0.wireOp",EDGE,"E12.0")}),1.0]])]});
            extrude(context, id + "F1", {"entities" : qUnion([Q0, Q1, Q2]), "depth" : 5 * mm});
        }
        {
            var Q0;
            Q0=makeQuery(id+"F1.opExtrude","CAP_FACE",FACE,{"disambiguationData":[OSD([sQuery(id+"F0.wireOp",EDGE,"E3"),sQuery(id+"F0.wireOp",EDGE,"E6"),sQuery(id+"F0.wireOp",EDGE,"E7"),sQuery(id+"F0.wireOp",EDGE,"E8"),sQuery(id+"F0.wireOp",EDGE,"E9.filletArc"),sQuery(id+"F0.wireOp",EDGE,"E10.filletArc"),sQuery(id+"F0.wireOp",EDGE,"E11.1.0"),sQuery(id+"F0.wireOp",EDGE,"E11.1.2"),sQuery(id+"F0.wireOp",EDGE,"E11.1.3"),sQuery(id+"F0.wireOp",EDGE,"E11.1.4"),sQuery(id+"F0.wireOp",EDGE,"E11.1.5"),sQuery(id+"F0.wireOp",EDGE,"E11.2.0"),sQuery(id+"F0.wireOp",EDGE,"E11.2.2"),sQuery(id+"F0.wireOp",EDGE,"E11.2.3"),sQuery(id+"F0.wireOp",EDGE,"E11.2.4"),sQuery(id+"F0.wireOp",EDGE,"E11.2.5"),sQuery(id+"F0.wireOp",EDGE,"E11.3.0"),sQuery(id+"F0.wireOp",EDGE,"E11.3.2"),sQuery(id+"F0.wireOp",EDGE,"E11.3.3"),sQuery(id+"F0.wireOp",EDGE,"E11.3.4"),sQuery(id+"F0.wireOp",EDGE,"E11.3.5"),sQuery(id+"F0.wireOp",EDGE,"E11.4.0"),sQuery(id+"F0.wireOp",EDGE,"E11.4.2"),sQuery(id+"F0.wireOp",EDGE,"E11.4.3"),sQuery(id+"F0.wireOp",EDGE,"E11.4.4"),sQuery(id+"F0.wireOp",EDGE,"E11.4.5"),sQuery(id+"F0.wireOp",EDGE,"E11.5.0"),sQuery(id+"F0.wireOp",EDGE,"E11.5.2"),sQuery(id+"F0.wireOp",EDGE,"E11.5.3"),sQuery(id+"F0.wireOp",EDGE,"E11.5.4"),sQuery(id+"F0.wireOp",EDGE,"E11.5.5"),sQuery(id+"F0.wireOp",EDGE,"E11.6.0"),sQuery(id+"F0.wireOp",EDGE,"E11.6.2"),sQuery(id+"F0.wireOp",EDGE,"E11.6.3"),sQuery(id+"F0.wireOp",EDGE,"E11.6.4"),sQuery(id+"F0.wireOp",EDGE,"E11.6.5"),sQuery(id+"F0.wireOp",EDGE,"E11.7.0"),sQuery(id+"F0.wireOp",EDGE,"E11.7.2"),sQuery(id+"F0.wireOp",EDGE,"E11.7.3"),sQuery(id+"F0.wireOp",EDGE,"E11.7.4"),sQuery(id+"F0.wireOp",EDGE,"E11.7.5"),sQuery(id+"F0.wireOp",EDGE,"E11.8.0"),sQuery(id+"F0.wireOp",EDGE,"E11.8.2"),sQuery(id+"F0.wireOp",EDGE,"E11.8.3"),sQuery(id+"F0.wireOp",EDGE,"E11.8.4"),sQuery(id+"F0.wireOp",EDGE,"E11.8.5"),sQuery(id+"F0.wireOp",EDGE,"E11.9.0"),sQuery(id+"F0.wireOp",EDGE,"E11.9.2"),sQuery(id+"F0.wireOp",EDGE,"E11.9.3"),sQuery(id+"F0.wireOp",EDGE,"E11.9.4"),sQuery(id+"F0.wireOp",EDGE,"E11.9.5"),sQuery(id+"F0.wireOp",EDGE,"E11.10.0"),sQuery(id+"F0.wireOp",EDGE,"E11.10.2"),sQuery(id+"F0.wireOp",EDGE,"E11.10.3"),sQuery(id+"F0.wireOp",EDGE,"E11.10.4"),sQuery(id+"F0.wireOp",EDGE,"E11.10.5"),sQuery(id+"F0.wireOp",EDGE,"E11.11.0"),sQuery(id+"F0.wireOp",EDGE,"E11.11.2"),sQuery(id+"F0.wireOp",EDGE,"E11.11.3"),sQuery(id+"F0.wireOp",EDGE,"E11.11.4"),sQuery(id+"F0.wireOp",EDGE,"E11.11.5"),sQuery(id+"F0.wireOp",EDGE,"E11.12.0"),sQuery(id+"F0.wireOp",EDGE,"E11.12.2"),sQuery(id+"F0.wireOp",EDGE,"E11.12.3"),sQuery(id+"F0.wireOp",EDGE,"E11.12.4"),sQuery(id+"F0.wireOp",EDGE,"E11.12.5"),sQuery(id+"F0.wireOp",EDGE,"E11.13.0"),sQuery(id+"F0.wireOp",EDGE,"E11.13.2"),sQuery(id+"F0.wireOp",EDGE,"E11.13.3"),sQuery(id+"F0.wireOp",EDGE,"E11.13.4"),sQuery(id+"F0.wireOp",EDGE,"E11.13.5"),sQuery(id+"F0.wireOp",EDGE,"E11.14.0"),sQuery(id+"F0.wireOp",EDGE,"E11.14.2"),sQuery(id+"F0.wireOp",EDGE,"E11.14.3"),sQuery(id+"F0.wireOp",EDGE,"E11.14.4"),sQuery(id+"F0.wireOp",EDGE,"E11.14.5"),sQuery(id+"F0.wireOp",EDGE,"E11.15.0"),sQuery(id+"F0.wireOp",EDGE,"E11.15.2"),sQuery(id+"F0.wireOp",EDGE,"E11.15.3"),sQuery(id+"F0.wireOp",EDGE,"E11.15.4"),sQuery(id+"F0.wireOp",EDGE,"E11.15.5"),sQuery(id+"F0.wireOp",EDGE,"E11.16.0"),sQuery(id+"F0.wireOp",EDGE,"E11.16.2"),sQuery(id+"F0.wireOp",EDGE,"E11.16.3"),sQuery(id+"F0.wireOp",EDGE,"E11.16.4"),sQuery(id+"F0.wireOp",EDGE,"E11.16.5"),sQuery(id+"F0.wireOp",EDGE,"E11.17.0"),sQuery(id+"F0.wireOp",EDGE,"E11.17.2"),sQuery(id+"F0.wireOp",EDGE,"E11.17.3"),sQuery(id+"F0.wireOp",EDGE,"E11.17.4"),sQuery(id+"F0.wireOp",EDGE,"E11.17.5"),sQuery(id+"F0.wireOp",EDGE,"E11.18.0"),sQuery(id+"F0.wireOp",EDGE,"E11.18.2"),sQuery(id+"F0.wireOp",EDGE,"E11.18.3"),sQuery(id+"F0.wireOp",EDGE,"E11.18.4"),sQuery(id+"F0.wireOp",EDGE,"E11.18.5"),sQuery(id+"F0.wireOp",EDGE,"E11.19.0"),sQuery(id+"F0.wireOp",EDGE,"E11.19.2"),sQuery(id+"F0.wireOp",EDGE,"E11.19.3"),sQuery(id+"F0.wireOp",EDGE,"E11.19.4"),sQuery(id+"F0.wireOp",EDGE,"E11.19.5"),sQuery(id+"F0.wireOp",EDGE,"E11.20.0"),sQuery(id+"F0.wireOp",EDGE,"E11.20.2"),sQuery(id+"F0.wireOp",EDGE,"E11.20.3"),sQuery(id+"F0.wireOp",EDGE,"E11.20.4"),sQuery(id+"F0.wireOp",EDGE,"E11.20.5"),sQuery(id+"F0.wireOp",EDGE,"E11.21.0"),sQuery(id+"F0.wireOp",EDGE,"E11.21.2"),sQuery(id+"F0.wireOp",EDGE,"E11.21.3"),sQuery(id+"F0.wireOp",EDGE,"E11.21.4"),sQuery(id+"F0.wireOp",EDGE,"E11.21.5"),sQuery(id+"F0.wireOp",EDGE,"E11.22.0"),sQuery(id+"F0.wireOp",EDGE,"E11.22.2"),sQuery(id+"F0.wireOp",EDGE,"E11.22.3"),sQuery(id+"F0.wireOp",EDGE,"E11.22.4"),sQuery(id+"F0.wireOp",EDGE,"E11.22.5"),sQuery(id+"F0.wireOp",EDGE,"E11.23.0"),sQuery(id+"F0.wireOp",EDGE,"E11.23.2"),sQuery(id+"F0.wireOp",EDGE,"E11.23.3"),sQuery(id+"F0.wireOp",EDGE,"E11.23.4"),sQuery(id+"F0.wireOp",EDGE,"E11.23.5"),sQuery(id+"F0.wireOp",EDGE,"E11.24.0"),sQuery(id+"F0.wireOp",EDGE,"E11.24.2"),sQuery(id+"F0.wireOp",EDGE,"E11.24.3"),sQuery(id+"F0.wireOp",EDGE,"E11.24.4"),sQuery(id+"F0.wireOp",EDGE,"E11.24.5"),sQuery(id+"F0.wireOp",EDGE,"E11.25.0"),sQuery(id+"F0.wireOp",EDGE,"E11.25.2"),sQuery(id+"F0.wireOp",EDGE,"E11.25.3"),sQuery(id+"F0.wireOp",EDGE,"E11.25.4"),sQuery(id+"F0.wireOp",EDGE,"E11.25.5"),sQuery(id+"F0.wireOp",EDGE,"E11.26.0"),sQuery(id+"F0.wireOp",EDGE,"E11.26.2"),sQuery(id+"F0.wireOp",EDGE,"E11.26.3"),sQuery(id+"F0.wireOp",EDGE,"E11.26.4"),sQuery(id+"F0.wireOp",EDGE,"E11.26.5"),sQuery(id+"F0.wireOp",EDGE,"E11.27.0"),sQuery(id+"F0.wireOp",EDGE,"E11.27.2"),sQuery(id+"F0.wireOp",EDGE,"E11.27.3"),sQuery(id+"F0.wireOp",EDGE,"E11.27.4"),sQuery(id+"F0.wireOp",EDGE,"E11.27.5"),sQuery(id+"F0.wireOp",EDGE,"E11.28.0"),sQuery(id+"F0.wireOp",EDGE,"E11.28.2"),sQuery(id+"F0.wireOp",EDGE,"E11.28.3"),sQuery(id+"F0.wireOp",EDGE,"E11.28.4"),sQuery(id+"F0.wireOp",EDGE,"E11.28.5"),sQuery(id+"F0.wireOp",EDGE,"E11.29.0"),sQuery(id+"F0.wireOp",EDGE,"E11.29.2"),sQuery(id+"F0.wireOp",EDGE,"E11.29.3"),sQuery(id+"F0.wireOp",EDGE,"E11.29.4"),sQuery(id+"F0.wireOp",EDGE,"E11.29.5"),sQuery(id+"F0.wireOp",EDGE,"E11.30.0"),sQuery(id+"F0.wireOp",EDGE,"E11.30.2"),sQuery(id+"F0.wireOp",EDGE,"E11.30.3"),sQuery(id+"F0.wireOp",EDGE,"E11.30.4"),sQuery(id+"F0.wireOp",EDGE,"E11.30.5"),sQuery(id+"F0.wireOp",EDGE,"E11.31.0"),sQuery(id+"F0.wireOp",EDGE,"E11.31.2"),sQuery(id+"F0.wireOp",EDGE,"E11.31.3"),sQuery(id+"F0.wireOp",EDGE,"E11.31.4"),sQuery(id+"F0.wireOp",EDGE,"E11.31.5"),sQuery(id+"F0.wireOp",EDGE,"E11.32.0"),sQuery(id+"F0.wireOp",EDGE,"E11.32.2"),sQuery(id+"F0.wireOp",EDGE,"E11.32.3"),sQuery(id+"F0.wireOp",EDGE,"E11.32.4"),sQuery(id+"F0.wireOp",EDGE,"E11.32.5"),sQuery(id+"F0.wireOp",EDGE,"E11.33.0"),sQuery(id+"F0.wireOp",EDGE,"E11.33.2"),sQuery(id+"F0.wireOp",EDGE,"E11.33.3"),sQuery(id+"F0.wireOp",EDGE,"E11.33.4"),sQuery(id+"F0.wireOp",EDGE,"E11.33.5"),sQuery(id+"F0.wireOp",EDGE,"E11.34.0"),sQuery(id+"F0.wireOp",EDGE,"E11.34.2"),sQuery(id+"F0.wireOp",EDGE,"E11.34.3"),sQuery(id+"F0.wireOp",EDGE,"E11.34.4"),sQuery(id+"F0.wireOp",EDGE,"E11.34.5"),sQuery(id+"F0.wireOp",EDGE,"E11.35.0"),sQuery(id+"F0.wireOp",EDGE,"E11.35.2"),sQuery(id+"F0.wireOp",EDGE,"E11.35.3"),sQuery(id+"F0.wireOp",EDGE,"E11.35.4"),sQuery(id+"F0.wireOp",EDGE,"E11.35.5"),sQuery(id+"F0.wireOp",EDGE,"E11.36.0"),sQuery(id+"F0.wireOp",EDGE,"E11.36.2"),sQuery(id+"F0.wireOp",EDGE,"E11.36.3"),sQuery(id+"F0.wireOp",EDGE,"E11.36.4"),sQuery(id+"F0.wireOp",EDGE,"E11.36.5"),sQuery(id+"F0.wireOp",EDGE,"E11.37.0"),sQuery(id+"F0.wireOp",EDGE,"E11.37.2"),sQuery(id+"F0.wireOp",EDGE,"E11.37.3"),sQuery(id+"F0.wireOp",EDGE,"E11.37.4"),sQuery(id+"F0.wireOp",EDGE,"E11.37.5"),sQuery(id+"F0.wireOp",EDGE,"E11.38.0"),sQuery(id+"F0.wireOp",EDGE,"E11.38.2"),sQuery(id+"F0.wireOp",EDGE,"E11.38.3"),sQuery(id+"F0.wireOp",EDGE,"E11.38.4"),sQuery(id+"F0.wireOp",EDGE,"E11.38.5"),sQuery(id+"F0.wireOp",EDGE,"E11.39.0"),sQuery(id+"F0.wireOp",EDGE,"E11.39.2"),sQuery(id+"F0.wireOp",EDGE,"E11.39.3"),sQuery(id+"F0.wireOp",EDGE,"E11.39.4"),sQuery(id+"F0.wireOp",EDGE,"E11.39.5"),sQuery(id+"F0.wireOp",EDGE,"E11.40.0"),sQuery(id+"F0.wireOp",EDGE,"E11.40.2"),sQuery(id+"F0.wireOp",EDGE,"E11.40.3"),sQuery(id+"F0.wireOp",EDGE,"E11.40.4"),sQuery(id+"F0.wireOp",EDGE,"E11.40.5"),sQuery(id+"F0.wireOp",EDGE,"E11.41.0"),sQuery(id+"F0.wireOp",EDGE,"E11.41.2"),sQuery(id+"F0.wireOp",EDGE,"E11.41.3"),sQuery(id+"F0.wireOp",EDGE,"E11.41.4"),sQuery(id+"F0.wireOp",EDGE,"E11.41.5"),sQuery(id+"F0.wireOp",EDGE,"E11.42.0"),sQuery(id+"F0.wireOp",EDGE,"E11.42.2"),sQuery(id+"F0.wireOp",EDGE,"E11.42.3"),sQuery(id+"F0.wireOp",EDGE,"E11.42.4"),sQuery(id+"F0.wireOp",EDGE,"E11.42.5"),sQuery(id+"F0.wireOp",EDGE,"E11.43.0"),sQuery(id+"F0.wireOp",EDGE,"E11.43.2"),sQuery(id+"F0.wireOp",EDGE,"E11.43.3"),sQuery(id+"F0.wireOp",EDGE,"E11.43.4"),sQuery(id+"F0.wireOp",EDGE,"E11.43.5"),sQuery(id+"F0.wireOp",EDGE,"E11.44.0"),sQuery(id+"F0.wireOp",EDGE,"E11.44.2"),sQuery(id+"F0.wireOp",EDGE,"E11.44.3"),sQuery(id+"F0.wireOp",EDGE,"E11.44.4"),sQuery(id+"F0.wireOp",EDGE,"E11.44.5"),sQuery(id+"F0.wireOp",EDGE,"E11.45.0"),sQuery(id+"F0.wireOp",EDGE,"E11.45.2"),sQuery(id+"F0.wireOp",EDGE,"E11.45.3"),sQuery(id+"F0.wireOp",EDGE,"E11.45.4"),sQuery(id+"F0.wireOp",EDGE,"E11.45.5"),sQuery(id+"F0.wireOp",EDGE,"E11.46.0"),sQuery(id+"F0.wireOp",EDGE,"E11.46.2"),sQuery(id+"F0.wireOp",EDGE,"E11.46.3"),sQuery(id+"F0.wireOp",EDGE,"E11.46.4"),sQuery(id+"F0.wireOp",EDGE,"E11.46.5"),sQuery(id+"F0.wireOp",EDGE,"E11.47.0"),sQuery(id+"F0.wireOp",EDGE,"E11.47.2"),sQuery(id+"F0.wireOp",EDGE,"E11.47.3"),sQuery(id+"F0.wireOp",EDGE,"E11.47.4"),sQuery(id+"F0.wireOp",EDGE,"E11.47.5"),sQuery(id+"F0.wireOp",EDGE,"E11.48.0"),sQuery(id+"F0.wireOp",EDGE,"E11.48.2"),sQuery(id+"F0.wireOp",EDGE,"E11.48.3"),sQuery(id+"F0.wireOp",EDGE,"E11.48.4"),sQuery(id+"F0.wireOp",EDGE,"E11.48.5"),sQuery(id+"F0.wireOp",EDGE,"E11.49.0"),sQuery(id+"F0.wireOp",EDGE,"E11.49.2"),sQuery(id+"F0.wireOp",EDGE,"E11.49.3"),sQuery(id+"F0.wireOp",EDGE,"E11.49.4"),sQuery(id+"F0.wireOp",EDGE,"E11.49.5"),sQuery(id+"F0.wireOp",EDGE,"E11.50.0"),sQuery(id+"F0.wireOp",EDGE,"E11.50.2"),sQuery(id+"F0.wireOp",EDGE,"E11.50.3"),sQuery(id+"F0.wireOp",EDGE,"E11.50.4"),sQuery(id+"F0.wireOp",EDGE,"E11.50.5"),sQuery(id+"F0.wireOp",EDGE,"E11.51.0"),sQuery(id+"F0.wireOp",EDGE,"E11.51.2"),sQuery(id+"F0.wireOp",EDGE,"E11.51.3"),sQuery(id+"F0.wireOp",EDGE,"E11.51.4"),sQuery(id+"F0.wireOp",EDGE,"E11.51.5"),sQuery(id+"F0.wireOp",EDGE,"E11.52.0"),sQuery(id+"F0.wireOp",EDGE,"E11.52.2"),sQuery(id+"F0.wireOp",EDGE,"E11.52.3"),sQuery(id+"F0.wireOp",EDGE,"E11.52.4"),sQuery(id+"F0.wireOp",EDGE,"E11.52.5"),sQuery(id+"F0.wireOp",EDGE,"E11.53.0"),sQuery(id+"F0.wireOp",EDGE,"E11.53.2"),sQuery(id+"F0.wireOp",EDGE,"E11.53.3"),sQuery(id+"F0.wireOp",EDGE,"E11.53.4"),sQuery(id+"F0.wireOp",EDGE,"E11.53.5"),sQuery(id+"F0.wireOp",EDGE,"E11.54.0"),sQuery(id+"F0.wireOp",EDGE,"E11.54.2"),sQuery(id+"F0.wireOp",EDGE,"E11.54.3"),sQuery(id+"F0.wireOp",EDGE,"E11.54.4"),sQuery(id+"F0.wireOp",EDGE,"E11.54.5"),sQuery(id+"F0.wireOp",EDGE,"E11.55.0"),sQuery(id+"F0.wireOp",EDGE,"E11.55.2"),sQuery(id+"F0.wireOp",EDGE,"E11.55.3"),sQuery(id+"F0.wireOp",EDGE,"E11.55.4"),sQuery(id+"F0.wireOp",EDGE,"E11.55.5"),sQuery(id+"F0.wireOp",EDGE,"E11.56.0"),sQuery(id+"F0.wireOp",EDGE,"E11.56.2"),sQuery(id+"F0.wireOp",EDGE,"E11.56.3"),sQuery(id+"F0.wireOp",EDGE,"E11.56.4"),sQuery(id+"F0.wireOp",EDGE,"E11.56.5"),sQuery(id+"F0.wireOp",EDGE,"E11.57.0"),sQuery(id+"F0.wireOp",EDGE,"E11.57.2"),sQuery(id+"F0.wireOp",EDGE,"E11.57.3"),sQuery(id+"F0.wireOp",EDGE,"E11.57.4"),sQuery(id+"F0.wireOp",EDGE,"E11.57.5"),sQuery(id+"F0.wireOp",EDGE,"E11.58.0"),sQuery(id+"F0.wireOp",EDGE,"E11.58.2"),sQuery(id+"F0.wireOp",EDGE,"E11.58.3"),sQuery(id+"F0.wireOp",EDGE,"E11.58.4"),sQuery(id+"F0.wireOp",EDGE,"E11.58.5"),sQuery(id+"F0.wireOp",EDGE,"E11.59.0"),sQuery(id+"F0.wireOp",EDGE,"E11.59.2"),sQuery(id+"F0.wireOp",EDGE,"E11.59.3"),sQuery(id+"F0.wireOp",EDGE,"E11.59.4"),sQuery(id+"F0.wireOp",EDGE,"E11.59.5"),sQuery(id+"F0.wireOp",EDGE,"E13")])],"isStart":false});
            var sketch = newSketch(context, id + "F2", { "sketchPlane" : qUnion([Q0])});
            skCircle(sketch, "E15.0", {"center": v(0, 0) * mm, "radius": 17.8 * mm});
            skCircle(sketch, "E16.0", {"center": v(0, 0) * mm, "radius": 25 * mm});
            skSolve(sketch);
        }
        {
            var Q0;
            Q0=makeQuery(id+"F2.imprint","IMPRINT",FACE,{"disambiguationData":[TD([[makeQuery(id+"F2.imprint","IMPRINT",EDGE,{"derivedFrom":sQuery(id+"F2.wireOp",EDGE,"E16.0")}),1.0]])]});
            var Q1;
            Q1=makeQuery(id+"F2.imprint","IMPRINT",FACE,{"disambiguationData":[TD([[makeQuery(id+"F2.imprint","IMPRINT",EDGE,{"derivedFrom":sQuery(id+"F2.wireOp",EDGE,"E15.0")}),-1.0]])]});
            var Q2;
            Q2=makeQuery(id+"F2.imprint","IMPRINT",FACE,{"disambiguationData":[TD([[makeQuery(id+"F2.imprint","IMPRINT",EDGE,{"derivedFrom":sQuery(id+"F2.wireOp",EDGE,"E15.0")}),1.0]])]});
            extrude(context, id + "F3", {"entities" : qUnion([Q0, Q1, Q2]), "operationType" : NewBodyOperationType.ADD, "depth" : 1 * mm});
        }
        {
            var Q0;
            Q0=makeQuery(id+"F3.opExtrude","CAP_FACE",FACE,{"disambiguationData":[OSD([sQuery(id+"F0.wireOp",EDGE,"E13"),sQuery(id+"F2.wireOp",EDGE,"E16.0")])],"isStart":false});
            var sketch = newSketch(context, id + "F4", { "sketchPlane" : qUnion([Q0])});
            skCircle(sketch, "E17", {"center": v(0, 0) * mm, "radius": 22 * mm});
            skCircle(sketch, "E18.0", {"center": v(0, 0) * mm, "radius": 10.9 * mm});
            skSolve(sketch);
        }
        {
            var Q0;
            Q0=makeQuery(id+"F4.imprint","IMPRINT",FACE,{"disambiguationData":[TD([[makeQuery(id+"F4.imprint","IMPRINT",EDGE,{"derivedFrom":sQuery(id+"F4.wireOp",EDGE,"E17")}),1.0]])]});
            extrude(context, id + "F5", {"entities" : qUnion([Q0]), "operationType" : NewBodyOperationType.REMOVE, "oppositeDirection" : true, "depth" : 4.5 * mm});
        }
        {
            var Q0;
            Q0=makeQuery(id+"F5.boolean.opBoolean","COPY",FACE,{"derivedFrom":makeQuery(id+"F5.opExtrude","CAP_FACE",FACE,{"disambiguationData":[OSD([sQuery(id+"F4.wireOp",EDGE,"E17"),sQuery(id+"F4.wireOp",EDGE,"E18.0")])],"isStart":false})});
            var sketch = newSketch(context, id + "F6", { "sketchPlane" : qUnion([Q0])});
            skCircle(sketch, "E19.0.0", {"center": v(0, 0) * mm, "radius": 22 * mm});
            skCircle(sketch, "E20.0", {"center": v(0, 0) * mm, "radius": 10.9 * mm});
            skCircle(sketch, "E21", {"center": v(0, 0) * mm, "radius": 11.85 * mm});
            skArc(sketch, "E22.0.endCap", {"start": v(-8.03, 8.73) * mm, "mid": v(-8.02, 8.73) * mm, "end": v(-8.02, 8.73) * mm});
            skLineSegment(sketch, "E22.0.left", {"start": v(-15.2, 15.9) * mm, "end": v(-8.03, 8.73) * mm});
            skLineSegment(sketch, "E22.0.right", {"start": v(-15.9, 15.2) * mm, "end": v(-8.73, 8.03) * mm});
            skArc(sketch, "E23.trimOffspring", {"start": v(-8.73, 8.02) * mm, "mid": v(-8.73, 8.02) * mm, "end": v(-8.73, 8.03) * mm});
            skLineSegment(sketch, "E24.1.0", {"start": v(-22, 0.5) * mm, "end": v(-11.85, 0.5) * mm});
            skLineSegment(sketch, "E24.1.1", {"start": v(-22, -0.5) * mm, "end": v(-11.85, -0.5) * mm});
            skArc(sketch, "E24.1.2", {"start": v(-11.85, 0.5) * mm, "mid": v(-11.84, 0.5) * mm, "end": v(-11.84, 0.5) * mm});
            skArc(sketch, "E24.1.3", {"start": v(-11.84, -0.5) * mm, "mid": v(-11.84, -0.5) * mm, "end": v(-11.85, -0.5) * mm});
            skLineSegment(sketch, "E24.2.0", {"start": v(-15.9, -15.2) * mm, "end": v(-8.73, -8.03) * mm});
            skLineSegment(sketch, "E24.2.1", {"start": v(-15.2, -15.9) * mm, "end": v(-8.03, -8.73) * mm});
            skArc(sketch, "E24.2.2", {"start": v(-8.73, -8.03) * mm, "mid": v(-8.73, -8.02) * mm, "end": v(-8.73, -8.02) * mm});
            skArc(sketch, "E24.2.3", {"start": v(-8.02, -8.73) * mm, "mid": v(-8.02, -8.73) * mm, "end": v(-8.03, -8.73) * mm});
            skLineSegment(sketch, "E24.3.0", {"start": v(-0.5, -22) * mm, "end": v(-0.5, -11.85) * mm});
            skLineSegment(sketch, "E24.3.1", {"start": v(0.5, -22) * mm, "end": v(0.5, -11.85) * mm});
            skArc(sketch, "E24.3.2", {"start": v(-0.5, -11.85) * mm, "mid": v(-0.5, -11.84) * mm, "end": v(-0.5, -11.84) * mm});
            skArc(sketch, "E24.3.3", {"start": v(0.5, -11.84) * mm, "mid": v(0.5, -11.84) * mm, "end": v(0.5, -11.85) * mm});
            skLineSegment(sketch, "E24.4.0", {"start": v(15.2, -15.9) * mm, "end": v(8.03, -8.73) * mm});
            skLineSegment(sketch, "E24.4.1", {"start": v(15.9, -15.2) * mm, "end": v(8.73, -8.03) * mm});
            skArc(sketch, "E24.4.2", {"start": v(8.03, -8.73) * mm, "mid": v(8.02, -8.73) * mm, "end": v(8.02, -8.73) * mm});
            skArc(sketch, "E24.4.3", {"start": v(8.73, -8.02) * mm, "mid": v(8.73, -8.02) * mm, "end": v(8.73, -8.03) * mm});
            skLineSegment(sketch, "E24.5.0", {"start": v(22, -0.5) * mm, "end": v(11.85, -0.5) * mm});
            skLineSegment(sketch, "E24.5.1", {"start": v(22, 0.5) * mm, "end": v(11.85, 0.5) * mm});
            skArc(sketch, "E24.5.2", {"start": v(11.85, -0.5) * mm, "mid": v(11.84, -0.5) * mm, "end": v(11.84, -0.5) * mm});
            skArc(sketch, "E24.5.3", {"start": v(11.84, 0.5) * mm, "mid": v(11.84, 0.5) * mm, "end": v(11.85, 0.5) * mm});
            skLineSegment(sketch, "E24.6.0", {"start": v(15.9, 15.2) * mm, "end": v(8.73, 8.03) * mm});
            skLineSegment(sketch, "E24.6.1", {"start": v(15.2, 15.9) * mm, "end": v(8.03, 8.73) * mm});
            skArc(sketch, "E24.6.2", {"start": v(8.73, 8.03) * mm, "mid": v(8.73, 8.02) * mm, "end": v(8.73, 8.02) * mm});
            skArc(sketch, "E24.6.3", {"start": v(8.02, 8.73) * mm, "mid": v(8.02, 8.73) * mm, "end": v(8.03, 8.73) * mm});
            skLineSegment(sketch, "E24.7.0", {"start": v(0.5, 22) * mm, "end": v(0.5, 11.85) * mm});
            skLineSegment(sketch, "E24.7.1", {"start": v(-0.5, 22) * mm, "end": v(-0.5, 11.85) * mm});
            skArc(sketch, "E24.7.2", {"start": v(0.5, 11.85) * mm, "mid": v(0.5, 11.84) * mm, "end": v(0.5, 11.84) * mm});
            skArc(sketch, "E24.7.3", {"start": v(-0.5, 11.84) * mm, "mid": v(-0.5, 11.84) * mm, "end": v(-0.5, 11.85) * mm});
            skPoint(sketch, "E25.orphan", {"position": v(-15.56, 14.85) * mm});
            skPoint(sketch, "E26.orphan", {"position": v(-14.85, 15.56) * mm});
            skPoint(sketch, "E27.orphan", {"position": v(-21.5, 0.5) * mm});
            skPoint(sketch, "E28.orphan", {"position": v(-21.5, -0.5) * mm});
            skPoint(sketch, "E29.orphan", {"position": v(14.85, 15.56) * mm});
            skPoint(sketch, "E30.orphan", {"position": v(15.56, 14.85) * mm});
            skPoint(sketch, "E31.orphan", {"position": v(-0.5, 21.5) * mm});
            skPoint(sketch, "E32.orphan", {"position": v(0.5, 21.5) * mm});
            skPoint(sketch, "E33.orphan", {"position": v(21.5, 0.5) * mm});
            skPoint(sketch, "E34.orphan", {"position": v(21.5, -0.5) * mm});
            skPoint(sketch, "E35.orphan", {"position": v(15.56, -14.85) * mm});
            skPoint(sketch, "E36.orphan", {"position": v(14.85, -15.56) * mm});
            skPoint(sketch, "E37.orphan", {"position": v(0.5, -21.5) * mm});
            skPoint(sketch, "E38.orphan", {"position": v(-0.5, -21.5) * mm});
            skPoint(sketch, "E39.orphan", {"position": v(-14.85, -15.56) * mm});
            skPoint(sketch, "E40.orphan", {"position": v(-15.56, -14.85) * mm});
            skSolve(sketch);
        }
        {
            var Q0;
            Q0=makeQuery(id+"F6.imprint","IMPRINT",FACE,{"disambiguationData":[TD([[makeQuery(id+"F6.imprint","IMPRINT",EDGE,{"derivedFrom":sQuery(id+"F6.wireOp",EDGE,"E20.0")}),-1.0]])]});
            var Q1;
            Q1=makeQuery(id+"F3.opExtrude","CAP_FACE",FACE,{"disambiguationData":[OSD([sQuery(id+"F0.wireOp",EDGE,"E13"),sQuery(id+"F2.wireOp",EDGE,"E16.0")])],"isStart":false});
            extrude(context, id + "F7", {"entities" : qUnion([Q0]), "operationType" : NewBodyOperationType.ADD, "endBound" : BoundingType.UP_TO_SURFACE, "endBoundEntityFace" : qUnion([Q1]), "depth" : 6 * mm});
        }
        {
            var Q0;
            {var subQ1=sQuery(id+"F6.wireOp",EDGE,"E22.0.endCap");Q0=makeQuery(id+"F6.imprint","IMPRINT",FACE,{"disambiguationData":[TD([[makeQuery(id+"F6.imprint","IMPRINT",EDGE,{"derivedFrom":subQ1}),-1.0]])]});}
            var Q1;
            {var subQ4=sQuery(id+"F6.wireOp",EDGE,"E24.7.2");Q1=makeQuery(id+"F6.imprint","IMPRINT",FACE,{"disambiguationData":[TD([[makeQuery(id+"F6.imprint","IMPRINT",EDGE,{"derivedFrom":subQ4}),-1.0]])]});}
            var Q2;
            {var subQ0=sQuery(id+"F6.wireOp",EDGE,"E24.6.2");Q2=makeQuery(id+"F6.imprint","IMPRINT",FACE,{"disambiguationData":[TD([[makeQuery(id+"F6.imprint","IMPRINT",EDGE,{"derivedFrom":subQ0}),-1.0]])]});}
            var Q3;
            {var subQ4=sQuery(id+"F6.wireOp",EDGE,"E24.5.2");Q3=makeQuery(id+"F6.imprint","IMPRINT",FACE,{"disambiguationData":[TD([[makeQuery(id+"F6.imprint","IMPRINT",EDGE,{"derivedFrom":subQ4}),-1.0]])]});}
            var Q4;
            {var subQ0=sQuery(id+"F6.wireOp",EDGE,"E24.4.2");Q4=makeQuery(id+"F6.imprint","IMPRINT",FACE,{"disambiguationData":[TD([[makeQuery(id+"F6.imprint","IMPRINT",EDGE,{"derivedFrom":subQ0}),-1.0]])]});}
            var Q5;
            {var subQ0=sQuery(id+"F6.wireOp",EDGE,"E24.3.2");Q5=makeQuery(id+"F6.imprint","IMPRINT",FACE,{"disambiguationData":[TD([[makeQuery(id+"F6.imprint","IMPRINT",EDGE,{"derivedFrom":subQ0}),-1.0]])]});}
            var Q6;
            {var subQ6=sQuery(id+"F6.wireOp",EDGE,"E24.2.2");Q6=makeQuery(id+"F6.imprint","IMPRINT",FACE,{"disambiguationData":[TD([[makeQuery(id+"F6.imprint","IMPRINT",EDGE,{"derivedFrom":subQ6}),-1.0]])]});}
            var Q7;
            {var subQ4=sQuery(id+"F6.wireOp",EDGE,"E24.1.2");Q7=makeQuery(id+"F6.imprint","IMPRINT",FACE,{"disambiguationData":[TD([[makeQuery(id+"F6.imprint","IMPRINT",EDGE,{"derivedFrom":subQ4}),-1.0]])]});}
            var Q8;
            Q8=makeQuery(id+"F3.opExtrude","CAP_FACE",FACE,{"disambiguationData":[OSD([sQuery(id+"F0.wireOp",EDGE,"E13"),sQuery(id+"F2.wireOp",EDGE,"E16.0")])],"isStart":false});
            extrude(context, id + "F8", {"entities" : qUnion([Q0, Q1, Q2, Q3, Q4, Q5, Q6, Q7]), "operationType" : NewBodyOperationType.ADD, "endBound" : BoundingType.UP_TO_SURFACE, "endBoundEntityFace" : qUnion([Q8]), "depth" : 6 * mm});
        }
        {
            var Q0;
            Q0=makeQuery(id+"F1.opExtrude","CAP_FACE",FACE,{"disambiguationData":[OSD([sQuery(id+"F0.wireOp",EDGE,"E3"),sQuery(id+"F0.wireOp",EDGE,"E6"),sQuery(id+"F0.wireOp",EDGE,"E7"),sQuery(id+"F0.wireOp",EDGE,"E8"),sQuery(id+"F0.wireOp",EDGE,"E9.filletArc"),sQuery(id+"F0.wireOp",EDGE,"E10.filletArc"),sQuery(id+"F0.wireOp",EDGE,"E11.1.0"),sQuery(id+"F0.wireOp",EDGE,"E11.1.2"),sQuery(id+"F0.wireOp",EDGE,"E11.1.3"),sQuery(id+"F0.wireOp",EDGE,"E11.1.4"),sQuery(id+"F0.wireOp",EDGE,"E11.1.5"),sQuery(id+"F0.wireOp",EDGE,"E11.2.0"),sQuery(id+"F0.wireOp",EDGE,"E11.2.2"),sQuery(id+"F0.wireOp",EDGE,"E11.2.3"),sQuery(id+"F0.wireOp",EDGE,"E11.2.4"),sQuery(id+"F0.wireOp",EDGE,"E11.2.5"),sQuery(id+"F0.wireOp",EDGE,"E11.3.0"),sQuery(id+"F0.wireOp",EDGE,"E11.3.2"),sQuery(id+"F0.wireOp",EDGE,"E11.3.3"),sQuery(id+"F0.wireOp",EDGE,"E11.3.4"),sQuery(id+"F0.wireOp",EDGE,"E11.3.5"),sQuery(id+"F0.wireOp",EDGE,"E11.4.0"),sQuery(id+"F0.wireOp",EDGE,"E11.4.2"),sQuery(id+"F0.wireOp",EDGE,"E11.4.3"),sQuery(id+"F0.wireOp",EDGE,"E11.4.4"),sQuery(id+"F0.wireOp",EDGE,"E11.4.5"),sQuery(id+"F0.wireOp",EDGE,"E11.5.0"),sQuery(id+"F0.wireOp",EDGE,"E11.5.2"),sQuery(id+"F0.wireOp",EDGE,"E11.5.3"),sQuery(id+"F0.wireOp",EDGE,"E11.5.4"),sQuery(id+"F0.wireOp",EDGE,"E11.5.5"),sQuery(id+"F0.wireOp",EDGE,"E11.6.0"),sQuery(id+"F0.wireOp",EDGE,"E11.6.2"),sQuery(id+"F0.wireOp",EDGE,"E11.6.3"),sQuery(id+"F0.wireOp",EDGE,"E11.6.4"),sQuery(id+"F0.wireOp",EDGE,"E11.6.5"),sQuery(id+"F0.wireOp",EDGE,"E11.7.0"),sQuery(id+"F0.wireOp",EDGE,"E11.7.2"),sQuery(id+"F0.wireOp",EDGE,"E11.7.3"),sQuery(id+"F0.wireOp",EDGE,"E11.7.4"),sQuery(id+"F0.wireOp",EDGE,"E11.7.5"),sQuery(id+"F0.wireOp",EDGE,"E11.8.0"),sQuery(id+"F0.wireOp",EDGE,"E11.8.2"),sQuery(id+"F0.wireOp",EDGE,"E11.8.3"),sQuery(id+"F0.wireOp",EDGE,"E11.8.4"),sQuery(id+"F0.wireOp",EDGE,"E11.8.5"),sQuery(id+"F0.wireOp",EDGE,"E11.9.0"),sQuery(id+"F0.wireOp",EDGE,"E11.9.2"),sQuery(id+"F0.wireOp",EDGE,"E11.9.3"),sQuery(id+"F0.wireOp",EDGE,"E11.9.4"),sQuery(id+"F0.wireOp",EDGE,"E11.9.5"),sQuery(id+"F0.wireOp",EDGE,"E11.10.0"),sQuery(id+"F0.wireOp",EDGE,"E11.10.2"),sQuery(id+"F0.wireOp",EDGE,"E11.10.3"),sQuery(id+"F0.wireOp",EDGE,"E11.10.4"),sQuery(id+"F0.wireOp",EDGE,"E11.10.5"),sQuery(id+"F0.wireOp",EDGE,"E11.11.0"),sQuery(id+"F0.wireOp",EDGE,"E11.11.2"),sQuery(id+"F0.wireOp",EDGE,"E11.11.3"),sQuery(id+"F0.wireOp",EDGE,"E11.11.4"),sQuery(id+"F0.wireOp",EDGE,"E11.11.5"),sQuery(id+"F0.wireOp",EDGE,"E11.12.0"),sQuery(id+"F0.wireOp",EDGE,"E11.12.2"),sQuery(id+"F0.wireOp",EDGE,"E11.12.3"),sQuery(id+"F0.wireOp",EDGE,"E11.12.4"),sQuery(id+"F0.wireOp",EDGE,"E11.12.5"),sQuery(id+"F0.wireOp",EDGE,"E11.13.0"),sQuery(id+"F0.wireOp",EDGE,"E11.13.2"),sQuery(id+"F0.wireOp",EDGE,"E11.13.3"),sQuery(id+"F0.wireOp",EDGE,"E11.13.4"),sQuery(id+"F0.wireOp",EDGE,"E11.13.5"),sQuery(id+"F0.wireOp",EDGE,"E11.14.0"),sQuery(id+"F0.wireOp",EDGE,"E11.14.2"),sQuery(id+"F0.wireOp",EDGE,"E11.14.3"),sQuery(id+"F0.wireOp",EDGE,"E11.14.4"),sQuery(id+"F0.wireOp",EDGE,"E11.14.5"),sQuery(id+"F0.wireOp",EDGE,"E11.15.0"),sQuery(id+"F0.wireOp",EDGE,"E11.15.2"),sQuery(id+"F0.wireOp",EDGE,"E11.15.3"),sQuery(id+"F0.wireOp",EDGE,"E11.15.4"),sQuery(id+"F0.wireOp",EDGE,"E11.15.5"),sQuery(id+"F0.wireOp",EDGE,"E11.16.0"),sQuery(id+"F0.wireOp",EDGE,"E11.16.2"),sQuery(id+"F0.wireOp",EDGE,"E11.16.3"),sQuery(id+"F0.wireOp",EDGE,"E11.16.4"),sQuery(id+"F0.wireOp",EDGE,"E11.16.5"),sQuery(id+"F0.wireOp",EDGE,"E11.17.0"),sQuery(id+"F0.wireOp",EDGE,"E11.17.2"),sQuery(id+"F0.wireOp",EDGE,"E11.17.3"),sQuery(id+"F0.wireOp",EDGE,"E11.17.4"),sQuery(id+"F0.wireOp",EDGE,"E11.17.5"),sQuery(id+"F0.wireOp",EDGE,"E11.18.0"),sQuery(id+"F0.wireOp",EDGE,"E11.18.2"),sQuery(id+"F0.wireOp",EDGE,"E11.18.3"),sQuery(id+"F0.wireOp",EDGE,"E11.18.4"),sQuery(id+"F0.wireOp",EDGE,"E11.18.5"),sQuery(id+"F0.wireOp",EDGE,"E11.19.0"),sQuery(id+"F0.wireOp",EDGE,"E11.19.2"),sQuery(id+"F0.wireOp",EDGE,"E11.19.3"),sQuery(id+"F0.wireOp",EDGE,"E11.19.4"),sQuery(id+"F0.wireOp",EDGE,"E11.19.5"),sQuery(id+"F0.wireOp",EDGE,"E11.20.0"),sQuery(id+"F0.wireOp",EDGE,"E11.20.2"),sQuery(id+"F0.wireOp",EDGE,"E11.20.3"),sQuery(id+"F0.wireOp",EDGE,"E11.20.4"),sQuery(id+"F0.wireOp",EDGE,"E11.20.5"),sQuery(id+"F0.wireOp",EDGE,"E11.21.0"),sQuery(id+"F0.wireOp",EDGE,"E11.21.2"),sQuery(id+"F0.wireOp",EDGE,"E11.21.3"),sQuery(id+"F0.wireOp",EDGE,"E11.21.4"),sQuery(id+"F0.wireOp",EDGE,"E11.21.5"),sQuery(id+"F0.wireOp",EDGE,"E11.22.0"),sQuery(id+"F0.wireOp",EDGE,"E11.22.2"),sQuery(id+"F0.wireOp",EDGE,"E11.22.3"),sQuery(id+"F0.wireOp",EDGE,"E11.22.4"),sQuery(id+"F0.wireOp",EDGE,"E11.22.5"),sQuery(id+"F0.wireOp",EDGE,"E11.23.0"),sQuery(id+"F0.wireOp",EDGE,"E11.23.2"),sQuery(id+"F0.wireOp",EDGE,"E11.23.3"),sQuery(id+"F0.wireOp",EDGE,"E11.23.4"),sQuery(id+"F0.wireOp",EDGE,"E11.23.5"),sQuery(id+"F0.wireOp",EDGE,"E11.24.0"),sQuery(id+"F0.wireOp",EDGE,"E11.24.2"),sQuery(id+"F0.wireOp",EDGE,"E11.24.3"),sQuery(id+"F0.wireOp",EDGE,"E11.24.4"),sQuery(id+"F0.wireOp",EDGE,"E11.24.5"),sQuery(id+"F0.wireOp",EDGE,"E11.25.0"),sQuery(id+"F0.wireOp",EDGE,"E11.25.2"),sQuery(id+"F0.wireOp",EDGE,"E11.25.3"),sQuery(id+"F0.wireOp",EDGE,"E11.25.4"),sQuery(id+"F0.wireOp",EDGE,"E11.25.5"),sQuery(id+"F0.wireOp",EDGE,"E11.26.0"),sQuery(id+"F0.wireOp",EDGE,"E11.26.2"),sQuery(id+"F0.wireOp",EDGE,"E11.26.3"),sQuery(id+"F0.wireOp",EDGE,"E11.26.4"),sQuery(id+"F0.wireOp",EDGE,"E11.26.5"),sQuery(id+"F0.wireOp",EDGE,"E11.27.0"),sQuery(id+"F0.wireOp",EDGE,"E11.27.2"),sQuery(id+"F0.wireOp",EDGE,"E11.27.3"),sQuery(id+"F0.wireOp",EDGE,"E11.27.4"),sQuery(id+"F0.wireOp",EDGE,"E11.27.5"),sQuery(id+"F0.wireOp",EDGE,"E11.28.0"),sQuery(id+"F0.wireOp",EDGE,"E11.28.2"),sQuery(id+"F0.wireOp",EDGE,"E11.28.3"),sQuery(id+"F0.wireOp",EDGE,"E11.28.4"),sQuery(id+"F0.wireOp",EDGE,"E11.28.5"),sQuery(id+"F0.wireOp",EDGE,"E11.29.0"),sQuery(id+"F0.wireOp",EDGE,"E11.29.2"),sQuery(id+"F0.wireOp",EDGE,"E11.29.3"),sQuery(id+"F0.wireOp",EDGE,"E11.29.4"),sQuery(id+"F0.wireOp",EDGE,"E11.29.5"),sQuery(id+"F0.wireOp",EDGE,"E11.30.0"),sQuery(id+"F0.wireOp",EDGE,"E11.30.2"),sQuery(id+"F0.wireOp",EDGE,"E11.30.3"),sQuery(id+"F0.wireOp",EDGE,"E11.30.4"),sQuery(id+"F0.wireOp",EDGE,"E11.30.5"),sQuery(id+"F0.wireOp",EDGE,"E11.31.0"),sQuery(id+"F0.wireOp",EDGE,"E11.31.2"),sQuery(id+"F0.wireOp",EDGE,"E11.31.3"),sQuery(id+"F0.wireOp",EDGE,"E11.31.4"),sQuery(id+"F0.wireOp",EDGE,"E11.31.5"),sQuery(id+"F0.wireOp",EDGE,"E11.32.0"),sQuery(id+"F0.wireOp",EDGE,"E11.32.2"),sQuery(id+"F0.wireOp",EDGE,"E11.32.3"),sQuery(id+"F0.wireOp",EDGE,"E11.32.4"),sQuery(id+"F0.wireOp",EDGE,"E11.32.5"),sQuery(id+"F0.wireOp",EDGE,"E11.33.0"),sQuery(id+"F0.wireOp",EDGE,"E11.33.2"),sQuery(id+"F0.wireOp",EDGE,"E11.33.3"),sQuery(id+"F0.wireOp",EDGE,"E11.33.4"),sQuery(id+"F0.wireOp",EDGE,"E11.33.5"),sQuery(id+"F0.wireOp",EDGE,"E11.34.0"),sQuery(id+"F0.wireOp",EDGE,"E11.34.2"),sQuery(id+"F0.wireOp",EDGE,"E11.34.3"),sQuery(id+"F0.wireOp",EDGE,"E11.34.4"),sQuery(id+"F0.wireOp",EDGE,"E11.34.5"),sQuery(id+"F0.wireOp",EDGE,"E11.35.0"),sQuery(id+"F0.wireOp",EDGE,"E11.35.2"),sQuery(id+"F0.wireOp",EDGE,"E11.35.3"),sQuery(id+"F0.wireOp",EDGE,"E11.35.4"),sQuery(id+"F0.wireOp",EDGE,"E11.35.5"),sQuery(id+"F0.wireOp",EDGE,"E11.36.0"),sQuery(id+"F0.wireOp",EDGE,"E11.36.2"),sQuery(id+"F0.wireOp",EDGE,"E11.36.3"),sQuery(id+"F0.wireOp",EDGE,"E11.36.4"),sQuery(id+"F0.wireOp",EDGE,"E11.36.5"),sQuery(id+"F0.wireOp",EDGE,"E11.37.0"),sQuery(id+"F0.wireOp",EDGE,"E11.37.2"),sQuery(id+"F0.wireOp",EDGE,"E11.37.3"),sQuery(id+"F0.wireOp",EDGE,"E11.37.4"),sQuery(id+"F0.wireOp",EDGE,"E11.37.5"),sQuery(id+"F0.wireOp",EDGE,"E11.38.0"),sQuery(id+"F0.wireOp",EDGE,"E11.38.2"),sQuery(id+"F0.wireOp",EDGE,"E11.38.3"),sQuery(id+"F0.wireOp",EDGE,"E11.38.4"),sQuery(id+"F0.wireOp",EDGE,"E11.38.5"),sQuery(id+"F0.wireOp",EDGE,"E11.39.0"),sQuery(id+"F0.wireOp",EDGE,"E11.39.2"),sQuery(id+"F0.wireOp",EDGE,"E11.39.3"),sQuery(id+"F0.wireOp",EDGE,"E11.39.4"),sQuery(id+"F0.wireOp",EDGE,"E11.39.5"),sQuery(id+"F0.wireOp",EDGE,"E11.40.0"),sQuery(id+"F0.wireOp",EDGE,"E11.40.2"),sQuery(id+"F0.wireOp",EDGE,"E11.40.3"),sQuery(id+"F0.wireOp",EDGE,"E11.40.4"),sQuery(id+"F0.wireOp",EDGE,"E11.40.5"),sQuery(id+"F0.wireOp",EDGE,"E11.41.0"),sQuery(id+"F0.wireOp",EDGE,"E11.41.2"),sQuery(id+"F0.wireOp",EDGE,"E11.41.3"),sQuery(id+"F0.wireOp",EDGE,"E11.41.4"),sQuery(id+"F0.wireOp",EDGE,"E11.41.5"),sQuery(id+"F0.wireOp",EDGE,"E11.42.0"),sQuery(id+"F0.wireOp",EDGE,"E11.42.2"),sQuery(id+"F0.wireOp",EDGE,"E11.42.3"),sQuery(id+"F0.wireOp",EDGE,"E11.42.4"),sQuery(id+"F0.wireOp",EDGE,"E11.42.5"),sQuery(id+"F0.wireOp",EDGE,"E11.43.0"),sQuery(id+"F0.wireOp",EDGE,"E11.43.2"),sQuery(id+"F0.wireOp",EDGE,"E11.43.3"),sQuery(id+"F0.wireOp",EDGE,"E11.43.4"),sQuery(id+"F0.wireOp",EDGE,"E11.43.5"),sQuery(id+"F0.wireOp",EDGE,"E11.44.0"),sQuery(id+"F0.wireOp",EDGE,"E11.44.2"),sQuery(id+"F0.wireOp",EDGE,"E11.44.3"),sQuery(id+"F0.wireOp",EDGE,"E11.44.4"),sQuery(id+"F0.wireOp",EDGE,"E11.44.5"),sQuery(id+"F0.wireOp",EDGE,"E11.45.0"),sQuery(id+"F0.wireOp",EDGE,"E11.45.2"),sQuery(id+"F0.wireOp",EDGE,"E11.45.3"),sQuery(id+"F0.wireOp",EDGE,"E11.45.4"),sQuery(id+"F0.wireOp",EDGE,"E11.45.5"),sQuery(id+"F0.wireOp",EDGE,"E11.46.0"),sQuery(id+"F0.wireOp",EDGE,"E11.46.2"),sQuery(id+"F0.wireOp",EDGE,"E11.46.3"),sQuery(id+"F0.wireOp",EDGE,"E11.46.4"),sQuery(id+"F0.wireOp",EDGE,"E11.46.5"),sQuery(id+"F0.wireOp",EDGE,"E11.47.0"),sQuery(id+"F0.wireOp",EDGE,"E11.47.2"),sQuery(id+"F0.wireOp",EDGE,"E11.47.3"),sQuery(id+"F0.wireOp",EDGE,"E11.47.4"),sQuery(id+"F0.wireOp",EDGE,"E11.47.5"),sQuery(id+"F0.wireOp",EDGE,"E11.48.0"),sQuery(id+"F0.wireOp",EDGE,"E11.48.2"),sQuery(id+"F0.wireOp",EDGE,"E11.48.3"),sQuery(id+"F0.wireOp",EDGE,"E11.48.4"),sQuery(id+"F0.wireOp",EDGE,"E11.48.5"),sQuery(id+"F0.wireOp",EDGE,"E11.49.0"),sQuery(id+"F0.wireOp",EDGE,"E11.49.2"),sQuery(id+"F0.wireOp",EDGE,"E11.49.3"),sQuery(id+"F0.wireOp",EDGE,"E11.49.4"),sQuery(id+"F0.wireOp",EDGE,"E11.49.5"),sQuery(id+"F0.wireOp",EDGE,"E11.50.0"),sQuery(id+"F0.wireOp",EDGE,"E11.50.2"),sQuery(id+"F0.wireOp",EDGE,"E11.50.3"),sQuery(id+"F0.wireOp",EDGE,"E11.50.4"),sQuery(id+"F0.wireOp",EDGE,"E11.50.5"),sQuery(id+"F0.wireOp",EDGE,"E11.51.0"),sQuery(id+"F0.wireOp",EDGE,"E11.51.2"),sQuery(id+"F0.wireOp",EDGE,"E11.51.3"),sQuery(id+"F0.wireOp",EDGE,"E11.51.4"),sQuery(id+"F0.wireOp",EDGE,"E11.51.5"),sQuery(id+"F0.wireOp",EDGE,"E11.52.0"),sQuery(id+"F0.wireOp",EDGE,"E11.52.2"),sQuery(id+"F0.wireOp",EDGE,"E11.52.3"),sQuery(id+"F0.wireOp",EDGE,"E11.52.4"),sQuery(id+"F0.wireOp",EDGE,"E11.52.5"),sQuery(id+"F0.wireOp",EDGE,"E11.53.0"),sQuery(id+"F0.wireOp",EDGE,"E11.53.2"),sQuery(id+"F0.wireOp",EDGE,"E11.53.3"),sQuery(id+"F0.wireOp",EDGE,"E11.53.4"),sQuery(id+"F0.wireOp",EDGE,"E11.53.5"),sQuery(id+"F0.wireOp",EDGE,"E11.54.0"),sQuery(id+"F0.wireOp",EDGE,"E11.54.2"),sQuery(id+"F0.wireOp",EDGE,"E11.54.3"),sQuery(id+"F0.wireOp",EDGE,"E11.54.4"),sQuery(id+"F0.wireOp",EDGE,"E11.54.5"),sQuery(id+"F0.wireOp",EDGE,"E11.55.0"),sQuery(id+"F0.wireOp",EDGE,"E11.55.2"),sQuery(id+"F0.wireOp",EDGE,"E11.55.3"),sQuery(id+"F0.wireOp",EDGE,"E11.55.4"),sQuery(id+"F0.wireOp",EDGE,"E11.55.5"),sQuery(id+"F0.wireOp",EDGE,"E11.56.0"),sQuery(id+"F0.wireOp",EDGE,"E11.56.2"),sQuery(id+"F0.wireOp",EDGE,"E11.56.3"),sQuery(id+"F0.wireOp",EDGE,"E11.56.4"),sQuery(id+"F0.wireOp",EDGE,"E11.56.5"),sQuery(id+"F0.wireOp",EDGE,"E11.57.0"),sQuery(id+"F0.wireOp",EDGE,"E11.57.2"),sQuery(id+"F0.wireOp",EDGE,"E11.57.3"),sQuery(id+"F0.wireOp",EDGE,"E11.57.4"),sQuery(id+"F0.wireOp",EDGE,"E11.57.5"),sQuery(id+"F0.wireOp",EDGE,"E11.58.0"),sQuery(id+"F0.wireOp",EDGE,"E11.58.2"),sQuery(id+"F0.wireOp",EDGE,"E11.58.3"),sQuery(id+"F0.wireOp",EDGE,"E11.58.4"),sQuery(id+"F0.wireOp",EDGE,"E11.58.5"),sQuery(id+"F0.wireOp",EDGE,"E11.59.0"),sQuery(id+"F0.wireOp",EDGE,"E11.59.2"),sQuery(id+"F0.wireOp",EDGE,"E11.59.3"),sQuery(id+"F0.wireOp",EDGE,"E11.59.4"),sQuery(id+"F0.wireOp",EDGE,"E11.59.5"),sQuery(id+"F0.wireOp",EDGE,"E13")])],"isStart":true});
            var sketch = newSketch(context, id + "F9", { "sketchPlane" : qUnion([Q0])});
            skCircle(sketch, "E41.0", {"center": v(0, 0) * mm, "radius": 10.9 * mm});
            skCircle(sketch, "E42.0", {"center": v(0, 0) * mm, "radius": 11.85 * mm});
            skSolve(sketch);
        }
        {
            var Q0;
            Q0=makeQuery(id+"F9.imprint","IMPRINT",FACE,{"disambiguationData":[TD([[makeQuery(id+"F9.imprint","IMPRINT",EDGE,{"derivedFrom":sQuery(id+"F9.wireOp",EDGE,"E41.0")}),1.0]])]});
            extrude(context, id + "F10", {"entities" : qUnion([Q0]), "operationType" : NewBodyOperationType.ADD, "depth" : 1 * mm});
        }
    });
